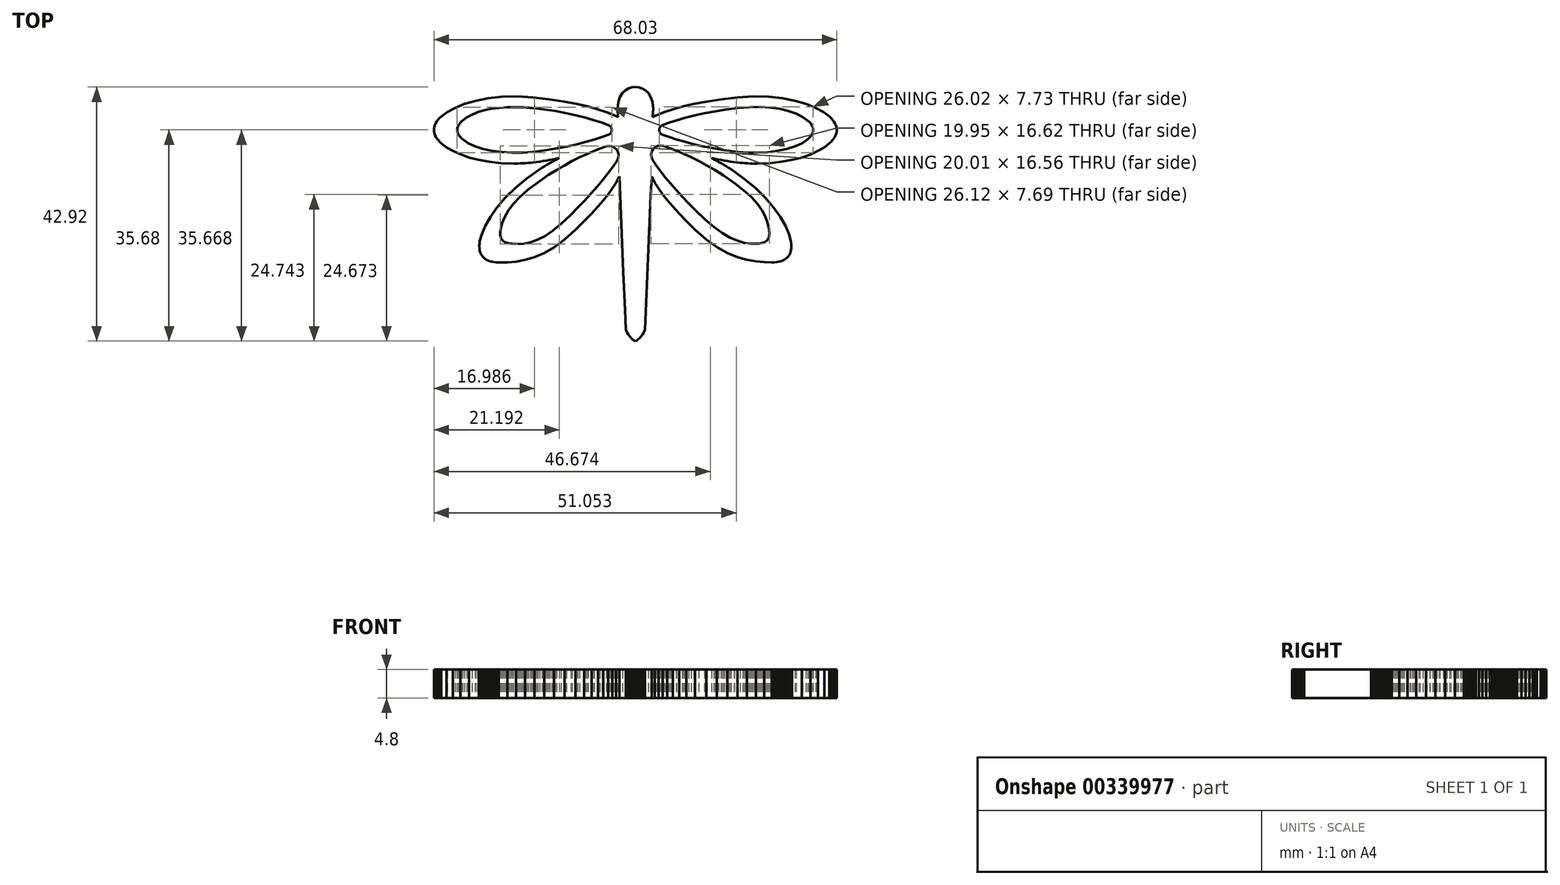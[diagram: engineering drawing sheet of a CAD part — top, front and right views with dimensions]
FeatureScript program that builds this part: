
annotation { "Feature Type Name" : "Feature", "Feature Type Description" : "" }
export const myFeature = defineFeature(function(context is Context, id is Id, definition is map)
    precondition{}
    {
        {
            var Q0;
            Q0=qCreatedBy(makeId("Top.planeOp"),FACE);
            var sketch = newSketch(context, id + "F0", { "sketchPlane" : qUnion([Q0])});
            skLineSegment(sketch, "E0", {"start": v(-35.15, 57.57) * mm, "end": v(-29.95, 57.76) * mm});
            skLineSegment(sketch, "E1", {"start": v(-29.95, 57.76) * mm, "end": v(-25.07, 58.28) * mm});
            skLineSegment(sketch, "E2", {"start": v(-25.07, 58.28) * mm, "end": v(-20.56, 59.1) * mm});
            skLineSegment(sketch, "E3", {"start": v(-20.56, 59.1) * mm, "end": v(-16.45, 60.17) * mm});
            skLineSegment(sketch, "E4", {"start": v(-16.45, 60.17) * mm, "end": v(-12.79, 61.45) * mm});
            skLineSegment(sketch, "E5", {"start": v(-12.79, 61.45) * mm, "end": v(-9.6, 62.89) * mm});
            skLineSegment(sketch, "E6", {"start": v(-9.6, 62.89) * mm, "end": v(-6.9, 64.45) * mm});
            skLineSegment(sketch, "E7", {"start": v(-6.9, 64.45) * mm, "end": v(-4.77, 66.09) * mm});
            skLineSegment(sketch, "E8", {"start": v(-4.77, 66.09) * mm, "end": v(-4.05, 66.78) * mm});
            skLineSegment(sketch, "E9", {"start": v(-4.05, 66.78) * mm, "end": v(-3.43, 67.48) * mm});
            skLineSegment(sketch, "E10", {"start": v(-3.43, 67.48) * mm, "end": v(-2.9, 68.2) * mm});
            skLineSegment(sketch, "E11", {"start": v(-2.9, 68.2) * mm, "end": v(-2.45, 68.9) * mm});
            skLineSegment(sketch, "E12", {"start": v(-2.45, 68.9) * mm, "end": v(-2.1, 69.62) * mm});
            skLineSegment(sketch, "E13", {"start": v(-2.1, 69.62) * mm, "end": v(-1.86, 70.34) * mm});
            skLineSegment(sketch, "E14", {"start": v(-1.86, 70.34) * mm, "end": v(-1.71, 71.06) * mm});
            skLineSegment(sketch, "E15", {"start": v(-1.71, 71.06) * mm, "end": v(-1.66, 71.78) * mm});
            skLineSegment(sketch, "E16", {"start": v(-1.66, 71.78) * mm, "end": v(-1.71, 72.48) * mm});
            skLineSegment(sketch, "E17", {"start": v(-1.71, 72.48) * mm, "end": v(-1.86, 73.2) * mm});
            skLineSegment(sketch, "E18", {"start": v(-1.86, 73.2) * mm, "end": v(-2.1, 73.9) * mm});
            skLineSegment(sketch, "E19", {"start": v(-2.1, 73.9) * mm, "end": v(-2.43, 74.61) * mm});
            skLineSegment(sketch, "E20", {"start": v(-2.43, 74.61) * mm, "end": v(-2.86, 75.32) * mm});
            skLineSegment(sketch, "E21", {"start": v(-2.86, 75.32) * mm, "end": v(-3.38, 76.02) * mm});
            skLineSegment(sketch, "E22", {"start": v(-3.38, 76.02) * mm, "end": v(-4, 76.7) * mm});
            skLineSegment(sketch, "E23", {"start": v(-4, 76.7) * mm, "end": v(-4.7, 77.39) * mm});
            skLineSegment(sketch, "E24", {"start": v(-4.7, 77.39) * mm, "end": v(-7.25, 79.3) * mm});
            skLineSegment(sketch, "E25", {"start": v(-7.25, 79.3) * mm, "end": v(-10.58, 81.11) * mm});
            skLineSegment(sketch, "E26", {"start": v(-10.58, 81.11) * mm, "end": v(-14.63, 82.73) * mm});
            skLineSegment(sketch, "E27", {"start": v(-14.63, 82.73) * mm, "end": v(-19.33, 84.1) * mm});
            skLineSegment(sketch, "E28", {"start": v(-19.33, 84.1) * mm, "end": v(-24.63, 85.12) * mm});
            skLineSegment(sketch, "E29", {"start": v(-24.63, 85.12) * mm, "end": v(-30.46, 85.75) * mm});
            skLineSegment(sketch, "E30", {"start": v(-30.46, 85.75) * mm, "end": v(-36.78, 85.9) * mm});
            skLineSegment(sketch, "E31", {"start": v(-36.78, 85.9) * mm, "end": v(-43.52, 85.52) * mm});
            skLineSegment(sketch, "E32", {"start": v(-43.52, 85.52) * mm, "end": v(-50.3, 84.72) * mm});
            skLineSegment(sketch, "E33", {"start": v(-50.3, 84.72) * mm, "end": v(-56.44, 83.78) * mm});
            skLineSegment(sketch, "E34", {"start": v(-56.44, 83.78) * mm, "end": v(-61.95, 82.73) * mm});
            skLineSegment(sketch, "E35", {"start": v(-61.95, 82.73) * mm, "end": v(-66.8, 81.61) * mm});
            skLineSegment(sketch, "E36", {"start": v(-66.8, 81.61) * mm, "end": v(-70.97, 80.47) * mm});
            skLineSegment(sketch, "E37", {"start": v(-70.97, 80.47) * mm, "end": v(-74.47, 79.34) * mm});
            skLineSegment(sketch, "E38", {"start": v(-74.47, 79.34) * mm, "end": v(-77.28, 78.26) * mm});
            skLineSegment(sketch, "E39", {"start": v(-77.28, 78.26) * mm, "end": v(-79.38, 77.3) * mm});
            skLineSegment(sketch, "E40", {"start": v(-79.38, 77.3) * mm, "end": v(-79.2, 80.74) * mm});
            skLineSegment(sketch, "E41", {"start": v(-79.2, 80.74) * mm, "end": v(-79.5, 83.53) * mm});
            skLineSegment(sketch, "E42", {"start": v(-79.5, 83.53) * mm, "end": v(-80.22, 85.73) * mm});
            skLineSegment(sketch, "E43", {"start": v(-80.22, 85.73) * mm, "end": v(-81.26, 87.4) * mm});
            skLineSegment(sketch, "E44", {"start": v(-81.26, 87.4) * mm, "end": v(-82.52, 88.6) * mm});
            skLineSegment(sketch, "E45", {"start": v(-82.52, 88.6) * mm, "end": v(-83.9, 89.37) * mm});
            skLineSegment(sketch, "E46", {"start": v(-83.9, 89.37) * mm, "end": v(-85.33, 89.8) * mm});
            skLineSegment(sketch, "E47", {"start": v(-85.33, 89.8) * mm, "end": v(-86.7, 89.92) * mm});
            skLineSegment(sketch, "E48", {"start": v(-86.7, 89.92) * mm, "end": v(-88.09, 89.79) * mm});
            skLineSegment(sketch, "E49", {"start": v(-88.09, 89.79) * mm, "end": v(-89.53, 89.35) * mm});
            skLineSegment(sketch, "E50", {"start": v(-89.53, 89.35) * mm, "end": v(-90.93, 88.55) * mm});
            skLineSegment(sketch, "E51", {"start": v(-90.93, 88.55) * mm, "end": v(-92.2, 87.34) * mm});
            skLineSegment(sketch, "E52", {"start": v(-92.2, 87.34) * mm, "end": v(-93.23, 85.66) * mm});
            skLineSegment(sketch, "E53", {"start": v(-93.23, 85.66) * mm, "end": v(-93.94, 83.46) * mm});
            skLineSegment(sketch, "E54", {"start": v(-93.94, 83.46) * mm, "end": v(-94.23, 80.7) * mm});
            skLineSegment(sketch, "E55", {"start": v(-94.23, 80.7) * mm, "end": v(-94.02, 77.3) * mm});
            skLineSegment(sketch, "E56", {"start": v(-94.02, 77.3) * mm, "end": v(-96.12, 78.27) * mm});
            skLineSegment(sketch, "E57", {"start": v(-96.12, 78.27) * mm, "end": v(-98.93, 79.34) * mm});
            skLineSegment(sketch, "E58", {"start": v(-98.93, 79.34) * mm, "end": v(-102.43, 80.47) * mm});
            skLineSegment(sketch, "E59", {"start": v(-102.43, 80.47) * mm, "end": v(-106.6, 81.61) * mm});
            skLineSegment(sketch, "E60", {"start": v(-106.6, 81.61) * mm, "end": v(-111.46, 82.73) * mm});
            skLineSegment(sketch, "E61", {"start": v(-111.46, 82.73) * mm, "end": v(-116.96, 83.78) * mm});
            skLineSegment(sketch, "E62", {"start": v(-116.96, 83.78) * mm, "end": v(-123.1, 84.73) * mm});
            skLineSegment(sketch, "E63", {"start": v(-123.1, 84.73) * mm, "end": v(-129.89, 85.52) * mm});
            skLineSegment(sketch, "E64", {"start": v(-129.89, 85.52) * mm, "end": v(-136.62, 85.91) * mm});
            skLineSegment(sketch, "E65", {"start": v(-136.62, 85.91) * mm, "end": v(-142.94, 85.76) * mm});
            skLineSegment(sketch, "E66", {"start": v(-142.94, 85.76) * mm, "end": v(-148.77, 85.13) * mm});
            skLineSegment(sketch, "E67", {"start": v(-148.77, 85.13) * mm, "end": v(-154.07, 84.1) * mm});
            skLineSegment(sketch, "E68", {"start": v(-154.07, 84.1) * mm, "end": v(-158.77, 82.73) * mm});
            skLineSegment(sketch, "E69", {"start": v(-158.77, 82.73) * mm, "end": v(-162.82, 81.11) * mm});
            skLineSegment(sketch, "E70", {"start": v(-162.82, 81.11) * mm, "end": v(-166.15, 79.3) * mm});
            skLineSegment(sketch, "E71", {"start": v(-166.15, 79.3) * mm, "end": v(-168.71, 77.39) * mm});
            skLineSegment(sketch, "E72", {"start": v(-168.71, 77.39) * mm, "end": v(-169.41, 76.7) * mm});
            skLineSegment(sketch, "E73", {"start": v(-169.41, 76.7) * mm, "end": v(-170.02, 76.02) * mm});
            skLineSegment(sketch, "E74", {"start": v(-170.02, 76.02) * mm, "end": v(-170.54, 75.32) * mm});
            skLineSegment(sketch, "E75", {"start": v(-170.54, 75.32) * mm, "end": v(-170.97, 74.61) * mm});
            skLineSegment(sketch, "E76", {"start": v(-170.97, 74.61) * mm, "end": v(-171.3, 73.9) * mm});
            skLineSegment(sketch, "E77", {"start": v(-171.3, 73.9) * mm, "end": v(-171.55, 73.2) * mm});
            skLineSegment(sketch, "E78", {"start": v(-171.55, 73.2) * mm, "end": v(-171.7, 72.48) * mm});
            skLineSegment(sketch, "E79", {"start": v(-171.7, 72.48) * mm, "end": v(-171.74, 71.78) * mm});
            skLineSegment(sketch, "E80", {"start": v(-171.74, 71.78) * mm, "end": v(-171.7, 71.06) * mm});
            skLineSegment(sketch, "E81", {"start": v(-171.7, 71.06) * mm, "end": v(-171.54, 70.34) * mm});
            skLineSegment(sketch, "E82", {"start": v(-171.54, 70.34) * mm, "end": v(-171.3, 69.62) * mm});
            skLineSegment(sketch, "E83", {"start": v(-171.3, 69.62) * mm, "end": v(-170.95, 68.9) * mm});
            skLineSegment(sketch, "E84", {"start": v(-170.95, 68.9) * mm, "end": v(-170.51, 68.2) * mm});
            skLineSegment(sketch, "E85", {"start": v(-170.51, 68.2) * mm, "end": v(-169.98, 67.48) * mm});
            skLineSegment(sketch, "E86", {"start": v(-169.98, 67.48) * mm, "end": v(-169.35, 66.78) * mm});
            skLineSegment(sketch, "E87", {"start": v(-169.35, 66.78) * mm, "end": v(-168.63, 66.1) * mm});
            skLineSegment(sketch, "E88", {"start": v(-168.63, 66.1) * mm, "end": v(-166.5, 64.45) * mm});
            skLineSegment(sketch, "E89", {"start": v(-166.5, 64.45) * mm, "end": v(-163.81, 62.89) * mm});
            skLineSegment(sketch, "E90", {"start": v(-163.81, 62.89) * mm, "end": v(-160.62, 61.45) * mm});
            skLineSegment(sketch, "E91", {"start": v(-160.62, 61.45) * mm, "end": v(-156.95, 60.17) * mm});
            skLineSegment(sketch, "E92", {"start": v(-156.95, 60.17) * mm, "end": v(-152.84, 59.1) * mm});
            skLineSegment(sketch, "E93", {"start": v(-152.84, 59.1) * mm, "end": v(-148.33, 58.28) * mm});
            skLineSegment(sketch, "E94", {"start": v(-148.33, 58.28) * mm, "end": v(-143.46, 57.76) * mm});
            skLineSegment(sketch, "E95", {"start": v(-143.46, 57.76) * mm, "end": v(-138.25, 57.58) * mm});
            skLineSegment(sketch, "E96", {"start": v(-138.25, 57.58) * mm, "end": v(-137.24, 57.58) * mm});
            skLineSegment(sketch, "E97", {"start": v(-137.24, 57.58) * mm, "end": v(-136.21, 57.6) * mm});
            skLineSegment(sketch, "E98", {"start": v(-136.21, 57.6) * mm, "end": v(-135.18, 57.64) * mm});
            skLineSegment(sketch, "E99", {"start": v(-135.18, 57.64) * mm, "end": v(-134.14, 57.69) * mm});
            skLineSegment(sketch, "E100", {"start": v(-134.14, 57.69) * mm, "end": v(-133.09, 57.75) * mm});
            skLineSegment(sketch, "E101", {"start": v(-133.09, 57.75) * mm, "end": v(-132.02, 57.83) * mm});
            skLineSegment(sketch, "E102", {"start": v(-132.02, 57.83) * mm, "end": v(-130.95, 57.92) * mm});
            skLineSegment(sketch, "E103", {"start": v(-130.95, 57.92) * mm, "end": v(-129.88, 58.03) * mm});
            skLineSegment(sketch, "E104", {"start": v(-129.88, 58.03) * mm, "end": v(-128.45, 58.2) * mm});
            skLineSegment(sketch, "E105", {"start": v(-128.45, 58.2) * mm, "end": v(-127.03, 58.39) * mm});
            skLineSegment(sketch, "E106", {"start": v(-127.03, 58.39) * mm, "end": v(-125.62, 58.6) * mm});
            skLineSegment(sketch, "E107", {"start": v(-125.62, 58.6) * mm, "end": v(-124.23, 58.82) * mm});
            skLineSegment(sketch, "E108", {"start": v(-124.23, 58.82) * mm, "end": v(-122.85, 59.07) * mm});
            skLineSegment(sketch, "E109", {"start": v(-122.85, 59.07) * mm, "end": v(-121.49, 59.33) * mm});
            skLineSegment(sketch, "E110", {"start": v(-121.49, 59.33) * mm, "end": v(-120.14, 59.6) * mm});
            skLineSegment(sketch, "E111", {"start": v(-120.14, 59.6) * mm, "end": v(-118.8, 59.9) * mm});
            skLineSegment(sketch, "E112", {"start": v(-118.8, 59.9) * mm, "end": v(-119.84, 59.36) * mm});
            skLineSegment(sketch, "E113", {"start": v(-119.84, 59.36) * mm, "end": v(-120.87, 58.81) * mm});
            skLineSegment(sketch, "E114", {"start": v(-120.87, 58.81) * mm, "end": v(-121.9, 58.24) * mm});
            skLineSegment(sketch, "E115", {"start": v(-121.9, 58.24) * mm, "end": v(-122.94, 57.66) * mm});
            skLineSegment(sketch, "E116", {"start": v(-122.94, 57.66) * mm, "end": v(-123.98, 57.06) * mm});
            skLineSegment(sketch, "E117", {"start": v(-123.98, 57.06) * mm, "end": v(-125, 56.45) * mm});
            skLineSegment(sketch, "E118", {"start": v(-125, 56.45) * mm, "end": v(-126.04, 55.81) * mm});
            skLineSegment(sketch, "E119", {"start": v(-126.04, 55.81) * mm, "end": v(-127.06, 55.16) * mm});
            skLineSegment(sketch, "E120", {"start": v(-127.06, 55.16) * mm, "end": v(-132.58, 51.27) * mm});
            skLineSegment(sketch, "E121", {"start": v(-132.58, 51.27) * mm, "end": v(-137.43, 47.22) * mm});
            skLineSegment(sketch, "E122", {"start": v(-137.43, 47.22) * mm, "end": v(-141.6, 43.1) * mm});
            skLineSegment(sketch, "E123", {"start": v(-141.6, 43.1) * mm, "end": v(-145.1, 38.99) * mm});
            skLineSegment(sketch, "E124", {"start": v(-145.1, 38.99) * mm, "end": v(-147.94, 35) * mm});
            skLineSegment(sketch, "E125", {"start": v(-147.94, 35) * mm, "end": v(-150.1, 31.21) * mm});
            skLineSegment(sketch, "E126", {"start": v(-150.1, 31.21) * mm, "end": v(-151.58, 27.72) * mm});
            skLineSegment(sketch, "E127", {"start": v(-151.58, 27.72) * mm, "end": v(-152.39, 24.63) * mm});
            skLineSegment(sketch, "E128", {"start": v(-152.39, 24.63) * mm, "end": v(-152.51, 23.66) * mm});
            skLineSegment(sketch, "E129", {"start": v(-152.51, 23.66) * mm, "end": v(-152.56, 22.74) * mm});
            skLineSegment(sketch, "E130", {"start": v(-152.56, 22.74) * mm, "end": v(-152.53, 21.87) * mm});
            skLineSegment(sketch, "E131", {"start": v(-152.53, 21.87) * mm, "end": v(-152.43, 21.05) * mm});
            skLineSegment(sketch, "E132", {"start": v(-152.43, 21.05) * mm, "end": v(-152.25, 20.29) * mm});
            skLineSegment(sketch, "E133", {"start": v(-152.25, 20.29) * mm, "end": v(-152, 19.58) * mm});
            skLineSegment(sketch, "E134", {"start": v(-152, 19.58) * mm, "end": v(-151.67, 18.93) * mm});
            skLineSegment(sketch, "E135", {"start": v(-151.67, 18.93) * mm, "end": v(-151.27, 18.35) * mm});
            skLineSegment(sketch, "E136", {"start": v(-151.27, 18.35) * mm, "end": v(-150.78, 17.82) * mm});
            skLineSegment(sketch, "E137", {"start": v(-150.78, 17.82) * mm, "end": v(-150.22, 17.35) * mm});
            skLineSegment(sketch, "E138", {"start": v(-150.22, 17.35) * mm, "end": v(-149.58, 16.95) * mm});
            skLineSegment(sketch, "E139", {"start": v(-149.58, 16.95) * mm, "end": v(-148.86, 16.6) * mm});
            skLineSegment(sketch, "E140", {"start": v(-148.86, 16.6) * mm, "end": v(-148.07, 16.31) * mm});
            skLineSegment(sketch, "E141", {"start": v(-148.07, 16.31) * mm, "end": v(-147.21, 16.09) * mm});
            skLineSegment(sketch, "E142", {"start": v(-147.21, 16.09) * mm, "end": v(-146.29, 15.93) * mm});
            skLineSegment(sketch, "E143", {"start": v(-146.29, 15.93) * mm, "end": v(-145.3, 15.83) * mm});
            skLineSegment(sketch, "E144", {"start": v(-145.3, 15.83) * mm, "end": v(-145.18, 15.83) * mm});
            skLineSegment(sketch, "E145", {"start": v(-145.18, 15.83) * mm, "end": v(-145.06, 15.82) * mm});
            skLineSegment(sketch, "E146", {"start": v(-145.06, 15.82) * mm, "end": v(-144.94, 15.82) * mm});
            skLineSegment(sketch, "E147", {"start": v(-144.94, 15.82) * mm, "end": v(-144.82, 15.81) * mm});
            skLineSegment(sketch, "E148", {"start": v(-144.82, 15.81) * mm, "end": v(-144.7, 15.81) * mm});
            skLineSegment(sketch, "E149", {"start": v(-144.7, 15.81) * mm, "end": v(-144.57, 15.8) * mm});
            skLineSegment(sketch, "E150", {"start": v(-144.57, 15.8) * mm, "end": v(-144.45, 15.8) * mm});
            skLineSegment(sketch, "E151", {"start": v(-144.45, 15.8) * mm, "end": v(-144.32, 15.8) * mm});
            skLineSegment(sketch, "E152", {"start": v(-144.32, 15.8) * mm, "end": v(-140.72, 15.84) * mm});
            skLineSegment(sketch, "E153", {"start": v(-140.72, 15.84) * mm, "end": v(-137.02, 16.15) * mm});
            skLineSegment(sketch, "E154", {"start": v(-137.02, 16.15) * mm, "end": v(-133.21, 16.84) * mm});
            skLineSegment(sketch, "E155", {"start": v(-133.21, 16.84) * mm, "end": v(-129.28, 18.02) * mm});
            skLineSegment(sketch, "E156", {"start": v(-129.28, 18.02) * mm, "end": v(-125.2, 19.78) * mm});
            skLineSegment(sketch, "E157", {"start": v(-125.2, 19.78) * mm, "end": v(-120.96, 22.23) * mm});
            skLineSegment(sketch, "E158", {"start": v(-120.96, 22.23) * mm, "end": v(-116.55, 25.49) * mm});
            skLineSegment(sketch, "E159", {"start": v(-116.55, 25.49) * mm, "end": v(-111.95, 29.65) * mm});
            skLineSegment(sketch, "E160", {"start": v(-111.95, 29.65) * mm, "end": v(-108.3, 33.29) * mm});
            skLineSegment(sketch, "E161", {"start": v(-108.3, 33.29) * mm, "end": v(-105.17, 36.52) * mm});
            skLineSegment(sketch, "E162", {"start": v(-105.17, 36.52) * mm, "end": v(-102.48, 39.42) * mm});
            skLineSegment(sketch, "E163", {"start": v(-102.48, 39.42) * mm, "end": v(-100.17, 42.08) * mm});
            skLineSegment(sketch, "E164", {"start": v(-100.17, 42.08) * mm, "end": v(-98.18, 44.59) * mm});
            skLineSegment(sketch, "E165", {"start": v(-98.18, 44.59) * mm, "end": v(-96.45, 47.03) * mm});
            skLineSegment(sketch, "E166", {"start": v(-96.45, 47.03) * mm, "end": v(-94.9, 49.5) * mm});
            skLineSegment(sketch, "E167", {"start": v(-94.9, 49.5) * mm, "end": v(-93.48, 52.09) * mm});
            skLineSegment(sketch, "E168", {"start": v(-93.48, 52.09) * mm, "end": v(-93.14, 44.02) * mm});
            skLineSegment(sketch, "E169", {"start": v(-93.14, 44.02) * mm, "end": v(-92.8, 35.96) * mm});
            skLineSegment(sketch, "E170", {"start": v(-92.8, 35.96) * mm, "end": v(-92.45, 27.9) * mm});
            skLineSegment(sketch, "E171", {"start": v(-92.45, 27.9) * mm, "end": v(-92.1, 19.83) * mm});
            skLineSegment(sketch, "E172", {"start": v(-92.1, 19.83) * mm, "end": v(-91.76, 11.77) * mm});
            skLineSegment(sketch, "E173", {"start": v(-91.76, 11.77) * mm, "end": v(-91.42, 3.7) * mm});
            skLineSegment(sketch, "E174", {"start": v(-91.42, 3.7) * mm, "end": v(-91.08, -4.36) * mm});
            skLineSegment(sketch, "E175", {"start": v(-91.08, -4.36) * mm, "end": v(-90.74, -12.42) * mm});
            skLineSegment(sketch, "E176", {"start": v(-90.74, -12.42) * mm, "end": v(-90.61, -12.95) * mm});
            skLineSegment(sketch, "E177", {"start": v(-90.61, -12.95) * mm, "end": v(-90.27, -13.65) * mm});
            skLineSegment(sketch, "E178", {"start": v(-90.27, -13.65) * mm, "end": v(-89.76, -14.47) * mm});
            skLineSegment(sketch, "E179", {"start": v(-89.76, -14.47) * mm, "end": v(-89.14, -15.3) * mm});
            skLineSegment(sketch, "E180", {"start": v(-89.14, -15.3) * mm, "end": v(-88.47, -16.1) * mm});
            skLineSegment(sketch, "E181", {"start": v(-88.47, -16.1) * mm, "end": v(-87.79, -16.76) * mm});
            skLineSegment(sketch, "E182", {"start": v(-87.79, -16.76) * mm, "end": v(-87.15, -17.22) * mm});
            skLineSegment(sketch, "E183", {"start": v(-87.15, -17.22) * mm, "end": v(-86.62, -17.38) * mm});
            skLineSegment(sketch, "E184", {"start": v(-86.62, -17.38) * mm, "end": v(-86.14, -17.22) * mm});
            skLineSegment(sketch, "E185", {"start": v(-86.14, -17.22) * mm, "end": v(-85.55, -16.76) * mm});
            skLineSegment(sketch, "E186", {"start": v(-85.55, -16.76) * mm, "end": v(-84.9, -16.1) * mm});
            skLineSegment(sketch, "E187", {"start": v(-84.9, -16.1) * mm, "end": v(-84.24, -15.3) * mm});
            skLineSegment(sketch, "E188", {"start": v(-84.24, -15.3) * mm, "end": v(-83.63, -14.47) * mm});
            skLineSegment(sketch, "E189", {"start": v(-83.63, -14.47) * mm, "end": v(-83.13, -13.65) * mm});
            skLineSegment(sketch, "E190", {"start": v(-83.13, -13.65) * mm, "end": v(-82.79, -12.95) * mm});
            skLineSegment(sketch, "E191", {"start": v(-82.79, -12.95) * mm, "end": v(-82.66, -12.42) * mm});
            skLineSegment(sketch, "E192", {"start": v(-82.66, -12.42) * mm, "end": v(-82.3, -4.36) * mm});
            skLineSegment(sketch, "E193", {"start": v(-82.3, -4.36) * mm, "end": v(-81.95, 3.7) * mm});
            skLineSegment(sketch, "E194", {"start": v(-81.95, 3.7) * mm, "end": v(-81.6, 11.77) * mm});
            skLineSegment(sketch, "E195", {"start": v(-81.6, 11.77) * mm, "end": v(-81.25, 19.84) * mm});
            skLineSegment(sketch, "E196", {"start": v(-81.25, 19.84) * mm, "end": v(-80.9, 27.9) * mm});
            skLineSegment(sketch, "E197", {"start": v(-80.9, 27.9) * mm, "end": v(-80.54, 35.97) * mm});
            skLineSegment(sketch, "E198", {"start": v(-80.54, 35.97) * mm, "end": v(-80.18, 44.03) * mm});
            skLineSegment(sketch, "E199", {"start": v(-80.18, 44.03) * mm, "end": v(-79.83, 52.1) * mm});
            skLineSegment(sketch, "E200", {"start": v(-79.83, 52.1) * mm, "end": v(-78.41, 49.51) * mm});
            skLineSegment(sketch, "E201", {"start": v(-78.41, 49.51) * mm, "end": v(-76.88, 47.04) * mm});
            skLineSegment(sketch, "E202", {"start": v(-76.88, 47.04) * mm, "end": v(-75.16, 44.6) * mm});
            skLineSegment(sketch, "E203", {"start": v(-75.16, 44.6) * mm, "end": v(-73.18, 42.08) * mm});
            skLineSegment(sketch, "E204", {"start": v(-73.18, 42.08) * mm, "end": v(-70.9, 39.42) * mm});
            skLineSegment(sketch, "E205", {"start": v(-70.9, 39.42) * mm, "end": v(-68.22, 36.52) * mm});
            skLineSegment(sketch, "E206", {"start": v(-68.22, 36.52) * mm, "end": v(-65.1, 33.3) * mm});
            skLineSegment(sketch, "E207", {"start": v(-65.1, 33.3) * mm, "end": v(-61.45, 29.65) * mm});
            skLineSegment(sketch, "E208", {"start": v(-61.45, 29.65) * mm, "end": v(-56.8, 25.5) * mm});
            skLineSegment(sketch, "E209", {"start": v(-56.8, 25.5) * mm, "end": v(-52.24, 22.26) * mm});
            skLineSegment(sketch, "E210", {"start": v(-52.24, 22.26) * mm, "end": v(-47.82, 19.82) * mm});
            skLineSegment(sketch, "E211", {"start": v(-47.82, 19.82) * mm, "end": v(-43.58, 18.08) * mm});
            skLineSegment(sketch, "E212", {"start": v(-43.58, 18.08) * mm, "end": v(-39.55, 16.92) * mm});
            skLineSegment(sketch, "E213", {"start": v(-39.55, 16.92) * mm, "end": v(-35.77, 16.23) * mm});
            skLineSegment(sketch, "E214", {"start": v(-35.77, 16.23) * mm, "end": v(-32.27, 15.9) * mm});
            skLineSegment(sketch, "E215", {"start": v(-32.27, 15.9) * mm, "end": v(-29.08, 15.8) * mm});
            skLineSegment(sketch, "E216", {"start": v(-29.08, 15.8) * mm, "end": v(-28.95, 15.8) * mm});
            skLineSegment(sketch, "E217", {"start": v(-28.95, 15.8) * mm, "end": v(-28.83, 15.8) * mm});
            skLineSegment(sketch, "E218", {"start": v(-28.83, 15.8) * mm, "end": v(-28.7, 15.81) * mm});
            skLineSegment(sketch, "E219", {"start": v(-28.7, 15.81) * mm, "end": v(-28.58, 15.81) * mm});
            skLineSegment(sketch, "E220", {"start": v(-28.58, 15.81) * mm, "end": v(-28.46, 15.82) * mm});
            skLineSegment(sketch, "E221", {"start": v(-28.46, 15.82) * mm, "end": v(-28.34, 15.82) * mm});
            skLineSegment(sketch, "E222", {"start": v(-28.34, 15.82) * mm, "end": v(-28.22, 15.83) * mm});
            skLineSegment(sketch, "E223", {"start": v(-28.22, 15.83) * mm, "end": v(-28.1, 15.83) * mm});
            skLineSegment(sketch, "E224", {"start": v(-28.1, 15.83) * mm, "end": v(-27.11, 15.93) * mm});
            skLineSegment(sketch, "E225", {"start": v(-27.11, 15.93) * mm, "end": v(-26.18, 16.09) * mm});
            skLineSegment(sketch, "E226", {"start": v(-26.18, 16.09) * mm, "end": v(-25.33, 16.31) * mm});
            skLineSegment(sketch, "E227", {"start": v(-25.33, 16.31) * mm, "end": v(-24.54, 16.6) * mm});
            skLineSegment(sketch, "E228", {"start": v(-24.54, 16.6) * mm, "end": v(-23.82, 16.95) * mm});
            skLineSegment(sketch, "E229", {"start": v(-23.82, 16.95) * mm, "end": v(-23.18, 17.35) * mm});
            skLineSegment(sketch, "E230", {"start": v(-23.18, 17.35) * mm, "end": v(-22.61, 17.82) * mm});
            skLineSegment(sketch, "E231", {"start": v(-22.61, 17.82) * mm, "end": v(-22.13, 18.35) * mm});
            skLineSegment(sketch, "E232", {"start": v(-22.13, 18.35) * mm, "end": v(-21.73, 18.93) * mm});
            skLineSegment(sketch, "E233", {"start": v(-21.73, 18.93) * mm, "end": v(-21.4, 19.58) * mm});
            skLineSegment(sketch, "E234", {"start": v(-21.4, 19.58) * mm, "end": v(-21.15, 20.29) * mm});
            skLineSegment(sketch, "E235", {"start": v(-21.15, 20.29) * mm, "end": v(-20.97, 21.05) * mm});
            skLineSegment(sketch, "E236", {"start": v(-20.97, 21.05) * mm, "end": v(-20.86, 21.87) * mm});
            skLineSegment(sketch, "E237", {"start": v(-20.86, 21.87) * mm, "end": v(-20.84, 22.74) * mm});
            skLineSegment(sketch, "E238", {"start": v(-20.84, 22.74) * mm, "end": v(-20.88, 23.66) * mm});
            skLineSegment(sketch, "E239", {"start": v(-20.88, 23.66) * mm, "end": v(-21, 24.63) * mm});
            skLineSegment(sketch, "E240", {"start": v(-21, 24.63) * mm, "end": v(-21.82, 27.72) * mm});
            skLineSegment(sketch, "E241", {"start": v(-21.82, 27.72) * mm, "end": v(-23.3, 31.2) * mm});
            skLineSegment(sketch, "E242", {"start": v(-23.3, 31.2) * mm, "end": v(-25.46, 35) * mm});
            skLineSegment(sketch, "E243", {"start": v(-25.46, 35) * mm, "end": v(-28.3, 38.99) * mm});
            skLineSegment(sketch, "E244", {"start": v(-28.3, 38.99) * mm, "end": v(-31.8, 43.1) * mm});
            skLineSegment(sketch, "E245", {"start": v(-31.8, 43.1) * mm, "end": v(-35.97, 47.22) * mm});
            skLineSegment(sketch, "E246", {"start": v(-35.97, 47.22) * mm, "end": v(-40.82, 51.27) * mm});
            skLineSegment(sketch, "E247", {"start": v(-40.82, 51.27) * mm, "end": v(-46.34, 55.16) * mm});
            skLineSegment(sketch, "E248", {"start": v(-46.34, 55.16) * mm, "end": v(-47.36, 55.8) * mm});
            skLineSegment(sketch, "E249", {"start": v(-47.36, 55.8) * mm, "end": v(-48.4, 56.44) * mm});
            skLineSegment(sketch, "E250", {"start": v(-48.4, 56.44) * mm, "end": v(-49.42, 57.06) * mm});
            skLineSegment(sketch, "E251", {"start": v(-49.42, 57.06) * mm, "end": v(-50.46, 57.66) * mm});
            skLineSegment(sketch, "E252", {"start": v(-50.46, 57.66) * mm, "end": v(-51.5, 58.24) * mm});
            skLineSegment(sketch, "E253", {"start": v(-51.5, 58.24) * mm, "end": v(-52.53, 58.8) * mm});
            skLineSegment(sketch, "E254", {"start": v(-52.53, 58.8) * mm, "end": v(-53.56, 59.36) * mm});
            skLineSegment(sketch, "E255", {"start": v(-53.56, 59.36) * mm, "end": v(-54.6, 59.9) * mm});
            skLineSegment(sketch, "E256", {"start": v(-54.6, 59.9) * mm, "end": v(-53.26, 59.6) * mm});
            skLineSegment(sketch, "E257", {"start": v(-53.26, 59.6) * mm, "end": v(-51.91, 59.33) * mm});
            skLineSegment(sketch, "E258", {"start": v(-51.91, 59.33) * mm, "end": v(-50.55, 59.07) * mm});
            skLineSegment(sketch, "E259", {"start": v(-50.55, 59.07) * mm, "end": v(-49.17, 58.82) * mm});
            skLineSegment(sketch, "E260", {"start": v(-49.17, 58.82) * mm, "end": v(-47.78, 58.6) * mm});
            skLineSegment(sketch, "E261", {"start": v(-47.78, 58.6) * mm, "end": v(-46.37, 58.39) * mm});
            skLineSegment(sketch, "E262", {"start": v(-46.37, 58.39) * mm, "end": v(-44.95, 58.2) * mm});
            skLineSegment(sketch, "E263", {"start": v(-44.95, 58.2) * mm, "end": v(-43.52, 58.03) * mm});
            skLineSegment(sketch, "E264", {"start": v(-43.52, 58.03) * mm, "end": v(-42.45, 57.92) * mm});
            skLineSegment(sketch, "E265", {"start": v(-42.45, 57.92) * mm, "end": v(-41.38, 57.83) * mm});
            skLineSegment(sketch, "E266", {"start": v(-41.38, 57.83) * mm, "end": v(-40.32, 57.75) * mm});
            skLineSegment(sketch, "E267", {"start": v(-40.32, 57.75) * mm, "end": v(-39.27, 57.69) * mm});
            skLineSegment(sketch, "E268", {"start": v(-39.27, 57.69) * mm, "end": v(-38.22, 57.64) * mm});
            skLineSegment(sketch, "E269", {"start": v(-38.22, 57.64) * mm, "end": v(-37.2, 57.6) * mm});
            skLineSegment(sketch, "E270", {"start": v(-37.2, 57.6) * mm, "end": v(-36.17, 57.58) * mm});
            skLineSegment(sketch, "E271", {"start": v(-36.17, 57.58) * mm, "end": v(-35.15, 57.57) * mm});
            skLineSegment(sketch, "E272", {"start": v(-43.37, 81) * mm, "end": v(-38.63, 81.4) * mm});
            skLineSegment(sketch, "E273", {"start": v(-38.63, 81.4) * mm, "end": v(-34.07, 81.47) * mm});
            skLineSegment(sketch, "E274", {"start": v(-34.07, 81.47) * mm, "end": v(-29.76, 81.23) * mm});
            skLineSegment(sketch, "E275", {"start": v(-29.76, 81.23) * mm, "end": v(-25.74, 80.67) * mm});
            skLineSegment(sketch, "E276", {"start": v(-25.74, 80.67) * mm, "end": v(-22.08, 79.82) * mm});
            skLineSegment(sketch, "E277", {"start": v(-22.08, 79.82) * mm, "end": v(-18.83, 78.7) * mm});
            skLineSegment(sketch, "E278", {"start": v(-18.83, 78.7) * mm, "end": v(-16.05, 77.29) * mm});
            skLineSegment(sketch, "E279", {"start": v(-16.05, 77.29) * mm, "end": v(-13.8, 75.63) * mm});
            skLineSegment(sketch, "E280", {"start": v(-13.8, 75.63) * mm, "end": v(-13.29, 75.14) * mm});
            skLineSegment(sketch, "E281", {"start": v(-13.29, 75.14) * mm, "end": v(-12.84, 74.64) * mm});
            skLineSegment(sketch, "E282", {"start": v(-12.84, 74.64) * mm, "end": v(-12.46, 74.15) * mm});
            skLineSegment(sketch, "E283", {"start": v(-12.46, 74.15) * mm, "end": v(-12.15, 73.66) * mm});
            skLineSegment(sketch, "E284", {"start": v(-12.15, 73.66) * mm, "end": v(-11.9, 73.18) * mm});
            skLineSegment(sketch, "E285", {"start": v(-11.9, 73.18) * mm, "end": v(-11.73, 72.7) * mm});
            skLineSegment(sketch, "E286", {"start": v(-11.73, 72.7) * mm, "end": v(-11.62, 72.24) * mm});
            skLineSegment(sketch, "E287", {"start": v(-11.62, 72.24) * mm, "end": v(-11.58, 71.78) * mm});
            skLineSegment(sketch, "E288", {"start": v(-11.58, 71.78) * mm, "end": v(-11.62, 71.31) * mm});
            skLineSegment(sketch, "E289", {"start": v(-11.62, 71.31) * mm, "end": v(-11.73, 70.84) * mm});
            skLineSegment(sketch, "E290", {"start": v(-11.73, 70.84) * mm, "end": v(-11.91, 70.36) * mm});
            skLineSegment(sketch, "E291", {"start": v(-11.91, 70.36) * mm, "end": v(-12.16, 69.86) * mm});
            skLineSegment(sketch, "E292", {"start": v(-12.16, 69.86) * mm, "end": v(-12.49, 69.37) * mm});
            skLineSegment(sketch, "E293", {"start": v(-12.49, 69.37) * mm, "end": v(-12.88, 68.87) * mm});
            skLineSegment(sketch, "E294", {"start": v(-12.88, 68.87) * mm, "end": v(-13.34, 68.37) * mm});
            skLineSegment(sketch, "E295", {"start": v(-13.34, 68.37) * mm, "end": v(-13.87, 67.86) * mm});
            skLineSegment(sketch, "E296", {"start": v(-13.87, 67.86) * mm, "end": v(-16.25, 66.2) * mm});
            skLineSegment(sketch, "E297", {"start": v(-16.25, 66.2) * mm, "end": v(-19.28, 64.82) * mm});
            skLineSegment(sketch, "E298", {"start": v(-19.28, 64.82) * mm, "end": v(-22.83, 63.73) * mm});
            skLineSegment(sketch, "E299", {"start": v(-22.83, 63.73) * mm, "end": v(-26.74, 62.92) * mm});
            skLineSegment(sketch, "E300", {"start": v(-26.74, 62.92) * mm, "end": v(-30.9, 62.4) * mm});
            skLineSegment(sketch, "E301", {"start": v(-30.9, 62.4) * mm, "end": v(-35.14, 62.16) * mm});
            skLineSegment(sketch, "E302", {"start": v(-35.14, 62.16) * mm, "end": v(-39.34, 62.21) * mm});
            skLineSegment(sketch, "E303", {"start": v(-39.34, 62.21) * mm, "end": v(-43.36, 62.55) * mm});
            skLineSegment(sketch, "E304", {"start": v(-43.36, 62.55) * mm, "end": v(-48.26, 63.16) * mm});
            skLineSegment(sketch, "E305", {"start": v(-48.26, 63.16) * mm, "end": v(-52.99, 63.92) * mm});
            skLineSegment(sketch, "E306", {"start": v(-52.99, 63.92) * mm, "end": v(-57.5, 64.78) * mm});
            skLineSegment(sketch, "E307", {"start": v(-57.5, 64.78) * mm, "end": v(-61.75, 65.72) * mm});
            skLineSegment(sketch, "E308", {"start": v(-61.75, 65.72) * mm, "end": v(-65.7, 66.73) * mm});
            skLineSegment(sketch, "E309", {"start": v(-65.7, 66.73) * mm, "end": v(-69.29, 67.76) * mm});
            skLineSegment(sketch, "E310", {"start": v(-69.29, 67.76) * mm, "end": v(-72.5, 68.8) * mm});
            skLineSegment(sketch, "E311", {"start": v(-72.5, 68.8) * mm, "end": v(-75.27, 69.8) * mm});
            skLineSegment(sketch, "E312", {"start": v(-75.27, 69.8) * mm, "end": v(-75.87, 70.15) * mm});
            skLineSegment(sketch, "E313", {"start": v(-75.87, 70.15) * mm, "end": v(-76.3, 70.63) * mm});
            skLineSegment(sketch, "E314", {"start": v(-76.3, 70.63) * mm, "end": v(-76.56, 71.19) * mm});
            skLineSegment(sketch, "E315", {"start": v(-76.56, 71.19) * mm, "end": v(-76.65, 71.8) * mm});
            skLineSegment(sketch, "E316", {"start": v(-76.65, 71.8) * mm, "end": v(-76.56, 72.4) * mm});
            skLineSegment(sketch, "E317", {"start": v(-76.56, 72.4) * mm, "end": v(-76.3, 72.97) * mm});
            skLineSegment(sketch, "E318", {"start": v(-76.3, 72.97) * mm, "end": v(-75.88, 73.45) * mm});
            skLineSegment(sketch, "E319", {"start": v(-75.88, 73.45) * mm, "end": v(-75.28, 73.8) * mm});
            skLineSegment(sketch, "E320", {"start": v(-75.28, 73.8) * mm, "end": v(-72.51, 74.82) * mm});
            skLineSegment(sketch, "E321", {"start": v(-72.51, 74.82) * mm, "end": v(-69.3, 75.87) * mm});
            skLineSegment(sketch, "E322", {"start": v(-69.3, 75.87) * mm, "end": v(-65.7, 76.9) * mm});
            skLineSegment(sketch, "E323", {"start": v(-65.7, 76.9) * mm, "end": v(-61.76, 77.91) * mm});
            skLineSegment(sketch, "E324", {"start": v(-61.76, 77.91) * mm, "end": v(-57.52, 78.85) * mm});
            skLineSegment(sketch, "E325", {"start": v(-57.52, 78.85) * mm, "end": v(-53, 79.7) * mm});
            skLineSegment(sketch, "E326", {"start": v(-53, 79.7) * mm, "end": v(-48.27, 80.43) * mm});
            skLineSegment(sketch, "E327", {"start": v(-48.27, 80.43) * mm, "end": v(-43.37, 81) * mm});
            skLineSegment(sketch, "E328", {"start": v(-30.93, 25.37) * mm, "end": v(-31.26, 25.02) * mm});
            skLineSegment(sketch, "E329", {"start": v(-31.26, 25.02) * mm, "end": v(-31.64, 24.71) * mm});
            skLineSegment(sketch, "E330", {"start": v(-31.64, 24.71) * mm, "end": v(-32.1, 24.44) * mm});
            skLineSegment(sketch, "E331", {"start": v(-32.1, 24.44) * mm, "end": v(-32.6, 24.21) * mm});
            skLineSegment(sketch, "E332", {"start": v(-32.6, 24.21) * mm, "end": v(-33.18, 24.02) * mm});
            skLineSegment(sketch, "E333", {"start": v(-33.18, 24.02) * mm, "end": v(-33.81, 23.87) * mm});
            skLineSegment(sketch, "E334", {"start": v(-33.81, 23.87) * mm, "end": v(-34.5, 23.76) * mm});
            skLineSegment(sketch, "E335", {"start": v(-34.5, 23.76) * mm, "end": v(-35.23, 23.7) * mm});
            skLineSegment(sketch, "E336", {"start": v(-35.23, 23.7) * mm, "end": v(-37.97, 23.7) * mm});
            skLineSegment(sketch, "E337", {"start": v(-37.97, 23.7) * mm, "end": v(-40.76, 24.11) * mm});
            skLineSegment(sketch, "E338", {"start": v(-40.76, 24.11) * mm, "end": v(-43.64, 24.96) * mm});
            skLineSegment(sketch, "E339", {"start": v(-43.64, 24.96) * mm, "end": v(-46.67, 26.3) * mm});
            skLineSegment(sketch, "E340", {"start": v(-46.67, 26.3) * mm, "end": v(-49.9, 28.21) * mm});
            skLineSegment(sketch, "E341", {"start": v(-49.9, 28.21) * mm, "end": v(-53.37, 30.72) * mm});
            skLineSegment(sketch, "E342", {"start": v(-53.37, 30.72) * mm, "end": v(-57.14, 33.9) * mm});
            skLineSegment(sketch, "E343", {"start": v(-57.14, 33.9) * mm, "end": v(-61.27, 37.8) * mm});
            skLineSegment(sketch, "E344", {"start": v(-61.27, 37.8) * mm, "end": v(-64.19, 40.73) * mm});
            skLineSegment(sketch, "E345", {"start": v(-64.19, 40.73) * mm, "end": v(-66.93, 43.6) * mm});
            skLineSegment(sketch, "E346", {"start": v(-66.93, 43.6) * mm, "end": v(-69.5, 46.4) * mm});
            skLineSegment(sketch, "E347", {"start": v(-69.5, 46.4) * mm, "end": v(-71.89, 49.11) * mm});
            skLineSegment(sketch, "E348", {"start": v(-71.89, 49.11) * mm, "end": v(-74.08, 51.75) * mm});
            skLineSegment(sketch, "E349", {"start": v(-74.08, 51.75) * mm, "end": v(-76.06, 54.3) * mm});
            skLineSegment(sketch, "E350", {"start": v(-76.06, 54.3) * mm, "end": v(-77.84, 56.77) * mm});
            skLineSegment(sketch, "E351", {"start": v(-77.84, 56.77) * mm, "end": v(-79.4, 59.14) * mm});
            skLineSegment(sketch, "E352", {"start": v(-79.4, 59.14) * mm, "end": v(-79.91, 60.34) * mm});
            skLineSegment(sketch, "E353", {"start": v(-79.91, 60.34) * mm, "end": v(-80, 61.55) * mm});
            skLineSegment(sketch, "E354", {"start": v(-80, 61.55) * mm, "end": v(-79.74, 62.7) * mm});
            skLineSegment(sketch, "E355", {"start": v(-79.74, 62.7) * mm, "end": v(-79.16, 63.7) * mm});
            skLineSegment(sketch, "E356", {"start": v(-79.16, 63.7) * mm, "end": v(-78.32, 64.51) * mm});
            skLineSegment(sketch, "E357", {"start": v(-78.32, 64.51) * mm, "end": v(-77.28, 65.05) * mm});
            skLineSegment(sketch, "E358", {"start": v(-77.28, 65.05) * mm, "end": v(-76.08, 65.25) * mm});
            skLineSegment(sketch, "E359", {"start": v(-76.08, 65.25) * mm, "end": v(-74.78, 65.05) * mm});
            skLineSegment(sketch, "E360", {"start": v(-74.78, 65.05) * mm, "end": v(-72.1, 64.13) * mm});
            skLineSegment(sketch, "E361", {"start": v(-72.1, 64.13) * mm, "end": v(-69.25, 63.02) * mm});
            skLineSegment(sketch, "E362", {"start": v(-69.25, 63.02) * mm, "end": v(-66.27, 61.74) * mm});
            skLineSegment(sketch, "E363", {"start": v(-66.27, 61.74) * mm, "end": v(-63.15, 60.28) * mm});
            skLineSegment(sketch, "E364", {"start": v(-63.15, 60.28) * mm, "end": v(-59.92, 58.63) * mm});
            skLineSegment(sketch, "E365", {"start": v(-59.92, 58.63) * mm, "end": v(-56.59, 56.8) * mm});
            skLineSegment(sketch, "E366", {"start": v(-56.59, 56.8) * mm, "end": v(-53.15, 54.8) * mm});
            skLineSegment(sketch, "E367", {"start": v(-53.15, 54.8) * mm, "end": v(-49.64, 52.6) * mm});
            skLineSegment(sketch, "E368", {"start": v(-49.64, 52.6) * mm, "end": v(-44.9, 49.36) * mm});
            skLineSegment(sketch, "E369", {"start": v(-44.9, 49.36) * mm, "end": v(-40.96, 46.3) * mm});
            skLineSegment(sketch, "E370", {"start": v(-40.96, 46.3) * mm, "end": v(-37.76, 43.37) * mm});
            skLineSegment(sketch, "E371", {"start": v(-37.76, 43.37) * mm, "end": v(-35.22, 40.56) * mm});
            skLineSegment(sketch, "E372", {"start": v(-35.22, 40.56) * mm, "end": v(-33.27, 37.83) * mm});
            skLineSegment(sketch, "E373", {"start": v(-33.27, 37.83) * mm, "end": v(-31.84, 35.15) * mm});
            skLineSegment(sketch, "E374", {"start": v(-31.84, 35.15) * mm, "end": v(-30.86, 32.5) * mm});
            skLineSegment(sketch, "E375", {"start": v(-30.86, 32.5) * mm, "end": v(-30.26, 29.84) * mm});
            skLineSegment(sketch, "E376", {"start": v(-30.26, 29.84) * mm, "end": v(-30.16, 29.12) * mm});
            skLineSegment(sketch, "E377", {"start": v(-30.16, 29.12) * mm, "end": v(-30.12, 28.45) * mm});
            skLineSegment(sketch, "E378", {"start": v(-30.12, 28.45) * mm, "end": v(-30.13, 27.82) * mm});
            skLineSegment(sketch, "E379", {"start": v(-30.13, 27.82) * mm, "end": v(-30.19, 27.23) * mm});
            skLineSegment(sketch, "E380", {"start": v(-30.19, 27.23) * mm, "end": v(-30.3, 26.69) * mm});
            skLineSegment(sketch, "E381", {"start": v(-30.3, 26.69) * mm, "end": v(-30.46, 26.2) * mm});
            skLineSegment(sketch, "E382", {"start": v(-30.46, 26.2) * mm, "end": v(-30.67, 25.76) * mm});
            skLineSegment(sketch, "E383", {"start": v(-30.67, 25.76) * mm, "end": v(-30.93, 25.37) * mm});
            skLineSegment(sketch, "E384", {"start": v(-138.72, 23.67) * mm, "end": v(-139.45, 23.73) * mm});
            skLineSegment(sketch, "E385", {"start": v(-139.45, 23.73) * mm, "end": v(-140.13, 23.84) * mm});
            skLineSegment(sketch, "E386", {"start": v(-140.13, 23.84) * mm, "end": v(-140.75, 23.99) * mm});
            skLineSegment(sketch, "E387", {"start": v(-140.75, 23.99) * mm, "end": v(-141.32, 24.18) * mm});
            skLineSegment(sketch, "E388", {"start": v(-141.32, 24.18) * mm, "end": v(-141.82, 24.4) * mm});
            skLineSegment(sketch, "E389", {"start": v(-141.82, 24.4) * mm, "end": v(-142.27, 24.67) * mm});
            skLineSegment(sketch, "E390", {"start": v(-142.27, 24.67) * mm, "end": v(-142.66, 24.98) * mm});
            skLineSegment(sketch, "E391", {"start": v(-142.66, 24.98) * mm, "end": v(-142.98, 25.32) * mm});
            skLineSegment(sketch, "E392", {"start": v(-142.98, 25.32) * mm, "end": v(-143.24, 25.7) * mm});
            skLineSegment(sketch, "E393", {"start": v(-143.24, 25.7) * mm, "end": v(-143.45, 26.14) * mm});
            skLineSegment(sketch, "E394", {"start": v(-143.45, 26.14) * mm, "end": v(-143.6, 26.63) * mm});
            skLineSegment(sketch, "E395", {"start": v(-143.6, 26.63) * mm, "end": v(-143.72, 27.17) * mm});
            skLineSegment(sketch, "E396", {"start": v(-143.72, 27.17) * mm, "end": v(-143.77, 27.75) * mm});
            skLineSegment(sketch, "E397", {"start": v(-143.77, 27.75) * mm, "end": v(-143.78, 28.38) * mm});
            skLineSegment(sketch, "E398", {"start": v(-143.78, 28.38) * mm, "end": v(-143.74, 29.04) * mm});
            skLineSegment(sketch, "E399", {"start": v(-143.74, 29.04) * mm, "end": v(-143.64, 29.75) * mm});
            skLineSegment(sketch, "E400", {"start": v(-143.64, 29.75) * mm, "end": v(-143, 32.4) * mm});
            skLineSegment(sketch, "E401", {"start": v(-143, 32.4) * mm, "end": v(-141.9, 35.08) * mm});
            skLineSegment(sketch, "E402", {"start": v(-141.9, 35.08) * mm, "end": v(-140.3, 37.8) * mm});
            skLineSegment(sketch, "E403", {"start": v(-140.3, 37.8) * mm, "end": v(-138.18, 40.59) * mm});
            skLineSegment(sketch, "E404", {"start": v(-138.18, 40.59) * mm, "end": v(-135.46, 43.46) * mm});
            skLineSegment(sketch, "E405", {"start": v(-135.46, 43.46) * mm, "end": v(-132.1, 46.42) * mm});
            skLineSegment(sketch, "E406", {"start": v(-132.1, 46.42) * mm, "end": v(-128.08, 49.5) * mm});
            skLineSegment(sketch, "E407", {"start": v(-128.08, 49.5) * mm, "end": v(-123.34, 52.73) * mm});
            skLineSegment(sketch, "E408", {"start": v(-123.34, 52.73) * mm, "end": v(-119.9, 54.88) * mm});
            skLineSegment(sketch, "E409", {"start": v(-119.9, 54.88) * mm, "end": v(-116.58, 56.84) * mm});
            skLineSegment(sketch, "E410", {"start": v(-116.58, 56.84) * mm, "end": v(-113.36, 58.6) * mm});
            skLineSegment(sketch, "E411", {"start": v(-113.36, 58.6) * mm, "end": v(-110.25, 60.19) * mm});
            skLineSegment(sketch, "E412", {"start": v(-110.25, 60.19) * mm, "end": v(-107.25, 61.6) * mm});
            skLineSegment(sketch, "E413", {"start": v(-107.25, 61.6) * mm, "end": v(-104.38, 62.82) * mm});
            skLineSegment(sketch, "E414", {"start": v(-104.38, 62.82) * mm, "end": v(-101.63, 63.89) * mm});
            skLineSegment(sketch, "E415", {"start": v(-101.63, 63.89) * mm, "end": v(-99.02, 64.79) * mm});
            skLineSegment(sketch, "E416", {"start": v(-99.02, 64.79) * mm, "end": v(-97.7, 65) * mm});
            skLineSegment(sketch, "E417", {"start": v(-97.7, 65) * mm, "end": v(-96.5, 64.8) * mm});
            skLineSegment(sketch, "E418", {"start": v(-96.5, 64.8) * mm, "end": v(-95.44, 64.25) * mm});
            skLineSegment(sketch, "E419", {"start": v(-95.44, 64.25) * mm, "end": v(-94.6, 63.43) * mm});
            skLineSegment(sketch, "E420", {"start": v(-94.6, 63.43) * mm, "end": v(-94.01, 62.4) * mm});
            skLineSegment(sketch, "E421", {"start": v(-94.01, 62.4) * mm, "end": v(-93.75, 61.25) * mm});
            skLineSegment(sketch, "E422", {"start": v(-93.75, 61.25) * mm, "end": v(-93.86, 60.03) * mm});
            skLineSegment(sketch, "E423", {"start": v(-93.86, 60.03) * mm, "end": v(-94.4, 58.82) * mm});
            skLineSegment(sketch, "E424", {"start": v(-94.4, 58.82) * mm, "end": v(-96.12, 56.28) * mm});
            skLineSegment(sketch, "E425", {"start": v(-96.12, 56.28) * mm, "end": v(-98.11, 53.6) * mm});
            skLineSegment(sketch, "E426", {"start": v(-98.11, 53.6) * mm, "end": v(-100.35, 50.78) * mm});
            skLineSegment(sketch, "E427", {"start": v(-100.35, 50.78) * mm, "end": v(-102.79, 47.87) * mm});
            skLineSegment(sketch, "E428", {"start": v(-102.79, 47.87) * mm, "end": v(-105.4, 44.9) * mm});
            skLineSegment(sketch, "E429", {"start": v(-105.4, 44.9) * mm, "end": v(-108.15, 41.9) * mm});
            skLineSegment(sketch, "E430", {"start": v(-108.15, 41.9) * mm, "end": v(-111.01, 38.91) * mm});
            skLineSegment(sketch, "E431", {"start": v(-111.01, 38.91) * mm, "end": v(-113.94, 35.96) * mm});
            skLineSegment(sketch, "E432", {"start": v(-113.94, 35.96) * mm, "end": v(-117.99, 32.17) * mm});
            skLineSegment(sketch, "E433", {"start": v(-117.99, 32.17) * mm, "end": v(-121.6, 29.21) * mm});
            skLineSegment(sketch, "E434", {"start": v(-121.6, 29.21) * mm, "end": v(-124.88, 27) * mm});
            skLineSegment(sketch, "E435", {"start": v(-124.88, 27) * mm, "end": v(-127.88, 25.42) * mm});
            skLineSegment(sketch, "E436", {"start": v(-127.88, 25.42) * mm, "end": v(-130.69, 24.39) * mm});
            skLineSegment(sketch, "E437", {"start": v(-130.69, 24.39) * mm, "end": v(-133.38, 23.82) * mm});
            skLineSegment(sketch, "E438", {"start": v(-133.38, 23.82) * mm, "end": v(-136.03, 23.6) * mm});
            skLineSegment(sketch, "E439", {"start": v(-136.03, 23.6) * mm, "end": v(-138.72, 23.67) * mm});
            skLineSegment(sketch, "E440", {"start": v(-130.05, 62.51) * mm, "end": v(-134.43, 62.2) * mm});
            skLineSegment(sketch, "E441", {"start": v(-134.43, 62.2) * mm, "end": v(-138.81, 62.17) * mm});
            skLineSegment(sketch, "E442", {"start": v(-138.81, 62.17) * mm, "end": v(-143.1, 62.41) * mm});
            skLineSegment(sketch, "E443", {"start": v(-143.1, 62.41) * mm, "end": v(-147.18, 62.93) * mm});
            skLineSegment(sketch, "E444", {"start": v(-147.18, 62.93) * mm, "end": v(-150.97, 63.73) * mm});
            skLineSegment(sketch, "E445", {"start": v(-150.97, 63.73) * mm, "end": v(-154.38, 64.8) * mm});
            skLineSegment(sketch, "E446", {"start": v(-154.38, 64.8) * mm, "end": v(-157.3, 66.18) * mm});
            skLineSegment(sketch, "E447", {"start": v(-157.3, 66.18) * mm, "end": v(-159.65, 67.85) * mm});
            skLineSegment(sketch, "E448", {"start": v(-159.65, 67.85) * mm, "end": v(-160.17, 68.35) * mm});
            skLineSegment(sketch, "E449", {"start": v(-160.17, 68.35) * mm, "end": v(-160.64, 68.86) * mm});
            skLineSegment(sketch, "E450", {"start": v(-160.64, 68.86) * mm, "end": v(-161.03, 69.36) * mm});
            skLineSegment(sketch, "E451", {"start": v(-161.03, 69.36) * mm, "end": v(-161.35, 69.86) * mm});
            skLineSegment(sketch, "E452", {"start": v(-161.35, 69.86) * mm, "end": v(-161.6, 70.35) * mm});
            skLineSegment(sketch, "E453", {"start": v(-161.6, 70.35) * mm, "end": v(-161.79, 70.84) * mm});
            skLineSegment(sketch, "E454", {"start": v(-161.79, 70.84) * mm, "end": v(-161.9, 71.31) * mm});
            skLineSegment(sketch, "E455", {"start": v(-161.9, 71.31) * mm, "end": v(-161.94, 71.78) * mm});
            skLineSegment(sketch, "E456", {"start": v(-161.94, 71.78) * mm, "end": v(-161.9, 72.24) * mm});
            skLineSegment(sketch, "E457", {"start": v(-161.9, 72.24) * mm, "end": v(-161.8, 72.7) * mm});
            skLineSegment(sketch, "E458", {"start": v(-161.8, 72.7) * mm, "end": v(-161.62, 73.19) * mm});
            skLineSegment(sketch, "E459", {"start": v(-161.62, 73.19) * mm, "end": v(-161.37, 73.67) * mm});
            skLineSegment(sketch, "E460", {"start": v(-161.37, 73.67) * mm, "end": v(-161.06, 74.16) * mm});
            skLineSegment(sketch, "E461", {"start": v(-161.06, 74.16) * mm, "end": v(-160.67, 74.65) * mm});
            skLineSegment(sketch, "E462", {"start": v(-160.67, 74.65) * mm, "end": v(-160.23, 75.15) * mm});
            skLineSegment(sketch, "E463", {"start": v(-160.23, 75.15) * mm, "end": v(-159.71, 75.64) * mm});
            skLineSegment(sketch, "E464", {"start": v(-159.71, 75.64) * mm, "end": v(-157.87, 77.06) * mm});
            skLineSegment(sketch, "E465", {"start": v(-157.87, 77.06) * mm, "end": v(-155.7, 78.26) * mm});
            skLineSegment(sketch, "E466", {"start": v(-155.7, 78.26) * mm, "end": v(-153.23, 79.27) * mm});
            skLineSegment(sketch, "E467", {"start": v(-153.23, 79.27) * mm, "end": v(-150.49, 80.07) * mm});
            skLineSegment(sketch, "E468", {"start": v(-150.49, 80.07) * mm, "end": v(-147.5, 80.69) * mm});
            skLineSegment(sketch, "E469", {"start": v(-147.5, 80.69) * mm, "end": v(-144.27, 81.1) * mm});
            skLineSegment(sketch, "E470", {"start": v(-144.27, 81.1) * mm, "end": v(-140.84, 81.35) * mm});
            skLineSegment(sketch, "E471", {"start": v(-140.84, 81.35) * mm, "end": v(-137.23, 81.4) * mm});
            skLineSegment(sketch, "E472", {"start": v(-137.23, 81.4) * mm, "end": v(-136.35, 81.39) * mm});
            skLineSegment(sketch, "E473", {"start": v(-136.35, 81.39) * mm, "end": v(-135.47, 81.37) * mm});
            skLineSegment(sketch, "E474", {"start": v(-135.47, 81.37) * mm, "end": v(-134.58, 81.34) * mm});
            skLineSegment(sketch, "E475", {"start": v(-134.58, 81.34) * mm, "end": v(-133.68, 81.3) * mm});
            skLineSegment(sketch, "E476", {"start": v(-133.68, 81.3) * mm, "end": v(-132.78, 81.25) * mm});
            skLineSegment(sketch, "E477", {"start": v(-132.78, 81.25) * mm, "end": v(-131.87, 81.2) * mm});
            skLineSegment(sketch, "E478", {"start": v(-131.87, 81.2) * mm, "end": v(-130.96, 81.12) * mm});
            skLineSegment(sketch, "E479", {"start": v(-130.96, 81.12) * mm, "end": v(-130.04, 81.04) * mm});
            skLineSegment(sketch, "E480", {"start": v(-130.04, 81.04) * mm, "end": v(-125.1, 80.46) * mm});
            skLineSegment(sketch, "E481", {"start": v(-125.1, 80.46) * mm, "end": v(-120.36, 79.73) * mm});
            skLineSegment(sketch, "E482", {"start": v(-120.36, 79.73) * mm, "end": v(-115.82, 78.87) * mm});
            skLineSegment(sketch, "E483", {"start": v(-115.82, 78.87) * mm, "end": v(-111.56, 77.92) * mm});
            skLineSegment(sketch, "E484", {"start": v(-111.56, 77.92) * mm, "end": v(-107.6, 76.91) * mm});
            skLineSegment(sketch, "E485", {"start": v(-107.6, 76.91) * mm, "end": v(-103.99, 75.87) * mm});
            skLineSegment(sketch, "E486", {"start": v(-103.99, 75.87) * mm, "end": v(-100.77, 74.82) * mm});
            skLineSegment(sketch, "E487", {"start": v(-100.77, 74.82) * mm, "end": v(-97.99, 73.79) * mm});
            skLineSegment(sketch, "E488", {"start": v(-97.99, 73.79) * mm, "end": v(-97.4, 73.44) * mm});
            skLineSegment(sketch, "E489", {"start": v(-97.4, 73.44) * mm, "end": v(-96.97, 72.96) * mm});
            skLineSegment(sketch, "E490", {"start": v(-96.97, 72.96) * mm, "end": v(-96.71, 72.4) * mm});
            skLineSegment(sketch, "E491", {"start": v(-96.71, 72.4) * mm, "end": v(-96.63, 71.8) * mm});
            skLineSegment(sketch, "E492", {"start": v(-96.63, 71.8) * mm, "end": v(-96.71, 71.19) * mm});
            skLineSegment(sketch, "E493", {"start": v(-96.71, 71.19) * mm, "end": v(-96.97, 70.63) * mm});
            skLineSegment(sketch, "E494", {"start": v(-96.97, 70.63) * mm, "end": v(-97.4, 70.15) * mm});
            skLineSegment(sketch, "E495", {"start": v(-97.4, 70.15) * mm, "end": v(-98, 69.8) * mm});
            skLineSegment(sketch, "E496", {"start": v(-98, 69.8) * mm, "end": v(-100.78, 68.8) * mm});
            skLineSegment(sketch, "E497", {"start": v(-100.78, 68.8) * mm, "end": v(-104, 67.76) * mm});
            skLineSegment(sketch, "E498", {"start": v(-104, 67.76) * mm, "end": v(-107.6, 66.72) * mm});
            skLineSegment(sketch, "E499", {"start": v(-107.6, 66.72) * mm, "end": v(-111.57, 65.71) * mm});
            skLineSegment(sketch, "E500", {"start": v(-111.57, 65.71) * mm, "end": v(-115.84, 64.76) * mm});
            skLineSegment(sketch, "E501", {"start": v(-115.84, 64.76) * mm, "end": v(-120.37, 63.9) * mm});
            skLineSegment(sketch, "E502", {"start": v(-120.37, 63.9) * mm, "end": v(-125.12, 63.13) * mm});
            skLineSegment(sketch, "E503", {"start": v(-125.12, 63.13) * mm, "end": v(-130.05, 62.51) * mm});
            skSolve(sketch);
        }
        {
            var Q0;
            Q0=makeQuery(id+"F0.imprint","IMPRINT",FACE,{"disambiguationData":[TD([[makeQuery(id+"F0.imprint","IMPRINT",EDGE,{"derivedFrom":sQuery(id+"F0.wireOp",EDGE,"E0")}),1.0]])]});
            extrude(context, id + "F1", {"entities" : qUnion([Q0]), "depth" : 12 * mm});
        }
        {
            var Q0;
            Q0=makeQuery(id+"F1.opExtrude","SWEPT_BODY",BODY,{"disambiguationData":[OSD([sQuery(id+"F0.wireOp",EDGE,"E0"),sQuery(id+"F0.wireOp",EDGE,"E1"),sQuery(id+"F0.wireOp",EDGE,"E2"),sQuery(id+"F0.wireOp",EDGE,"E3"),sQuery(id+"F0.wireOp",EDGE,"E4"),sQuery(id+"F0.wireOp",EDGE,"E5"),sQuery(id+"F0.wireOp",EDGE,"E6"),sQuery(id+"F0.wireOp",EDGE,"E7"),sQuery(id+"F0.wireOp",EDGE,"E8"),sQuery(id+"F0.wireOp",EDGE,"E9"),sQuery(id+"F0.wireOp",EDGE,"E10"),sQuery(id+"F0.wireOp",EDGE,"E11"),sQuery(id+"F0.wireOp",EDGE,"E12"),sQuery(id+"F0.wireOp",EDGE,"E13"),sQuery(id+"F0.wireOp",EDGE,"E14"),sQuery(id+"F0.wireOp",EDGE,"E15"),sQuery(id+"F0.wireOp",EDGE,"E16"),sQuery(id+"F0.wireOp",EDGE,"E17"),sQuery(id+"F0.wireOp",EDGE,"E18"),sQuery(id+"F0.wireOp",EDGE,"E19"),sQuery(id+"F0.wireOp",EDGE,"E20"),sQuery(id+"F0.wireOp",EDGE,"E21"),sQuery(id+"F0.wireOp",EDGE,"E22"),sQuery(id+"F0.wireOp",EDGE,"E23"),sQuery(id+"F0.wireOp",EDGE,"E24"),sQuery(id+"F0.wireOp",EDGE,"E25"),sQuery(id+"F0.wireOp",EDGE,"E26"),sQuery(id+"F0.wireOp",EDGE,"E27"),sQuery(id+"F0.wireOp",EDGE,"E28"),sQuery(id+"F0.wireOp",EDGE,"E29"),sQuery(id+"F0.wireOp",EDGE,"E30"),sQuery(id+"F0.wireOp",EDGE,"E31"),sQuery(id+"F0.wireOp",EDGE,"E32"),sQuery(id+"F0.wireOp",EDGE,"E33"),sQuery(id+"F0.wireOp",EDGE,"E34"),sQuery(id+"F0.wireOp",EDGE,"E35"),sQuery(id+"F0.wireOp",EDGE,"E36"),sQuery(id+"F0.wireOp",EDGE,"E37"),sQuery(id+"F0.wireOp",EDGE,"E38"),sQuery(id+"F0.wireOp",EDGE,"E39"),sQuery(id+"F0.wireOp",EDGE,"E40"),sQuery(id+"F0.wireOp",EDGE,"E41"),sQuery(id+"F0.wireOp",EDGE,"E42"),sQuery(id+"F0.wireOp",EDGE,"E43"),sQuery(id+"F0.wireOp",EDGE,"E44"),sQuery(id+"F0.wireOp",EDGE,"E45"),sQuery(id+"F0.wireOp",EDGE,"E46"),sQuery(id+"F0.wireOp",EDGE,"E47"),sQuery(id+"F0.wireOp",EDGE,"E48"),sQuery(id+"F0.wireOp",EDGE,"E49"),sQuery(id+"F0.wireOp",EDGE,"E50"),sQuery(id+"F0.wireOp",EDGE,"E51"),sQuery(id+"F0.wireOp",EDGE,"E52"),sQuery(id+"F0.wireOp",EDGE,"E53"),sQuery(id+"F0.wireOp",EDGE,"E54"),sQuery(id+"F0.wireOp",EDGE,"E55"),sQuery(id+"F0.wireOp",EDGE,"E56"),sQuery(id+"F0.wireOp",EDGE,"E57"),sQuery(id+"F0.wireOp",EDGE,"E58"),sQuery(id+"F0.wireOp",EDGE,"E59"),sQuery(id+"F0.wireOp",EDGE,"E60"),sQuery(id+"F0.wireOp",EDGE,"E61"),sQuery(id+"F0.wireOp",EDGE,"E62"),sQuery(id+"F0.wireOp",EDGE,"E63"),sQuery(id+"F0.wireOp",EDGE,"E64"),sQuery(id+"F0.wireOp",EDGE,"E65"),sQuery(id+"F0.wireOp",EDGE,"E66"),sQuery(id+"F0.wireOp",EDGE,"E67"),sQuery(id+"F0.wireOp",EDGE,"E68"),sQuery(id+"F0.wireOp",EDGE,"E69"),sQuery(id+"F0.wireOp",EDGE,"E70"),sQuery(id+"F0.wireOp",EDGE,"E71"),sQuery(id+"F0.wireOp",EDGE,"E72"),sQuery(id+"F0.wireOp",EDGE,"E73"),sQuery(id+"F0.wireOp",EDGE,"E74"),sQuery(id+"F0.wireOp",EDGE,"E75"),sQuery(id+"F0.wireOp",EDGE,"E76"),sQuery(id+"F0.wireOp",EDGE,"E77"),sQuery(id+"F0.wireOp",EDGE,"E78"),sQuery(id+"F0.wireOp",EDGE,"E79"),sQuery(id+"F0.wireOp",EDGE,"E80"),sQuery(id+"F0.wireOp",EDGE,"E81"),sQuery(id+"F0.wireOp",EDGE,"E82"),sQuery(id+"F0.wireOp",EDGE,"E83"),sQuery(id+"F0.wireOp",EDGE,"E84"),sQuery(id+"F0.wireOp",EDGE,"E85"),sQuery(id+"F0.wireOp",EDGE,"E86"),sQuery(id+"F0.wireOp",EDGE,"E87"),sQuery(id+"F0.wireOp",EDGE,"E88"),sQuery(id+"F0.wireOp",EDGE,"E89"),sQuery(id+"F0.wireOp",EDGE,"E90"),sQuery(id+"F0.wireOp",EDGE,"E91"),sQuery(id+"F0.wireOp",EDGE,"E92"),sQuery(id+"F0.wireOp",EDGE,"E93"),sQuery(id+"F0.wireOp",EDGE,"E94"),sQuery(id+"F0.wireOp",EDGE,"E95"),sQuery(id+"F0.wireOp",EDGE,"E96"),sQuery(id+"F0.wireOp",EDGE,"E97"),sQuery(id+"F0.wireOp",EDGE,"E98"),sQuery(id+"F0.wireOp",EDGE,"E99"),sQuery(id+"F0.wireOp",EDGE,"E100"),sQuery(id+"F0.wireOp",EDGE,"E101"),sQuery(id+"F0.wireOp",EDGE,"E102"),sQuery(id+"F0.wireOp",EDGE,"E103"),sQuery(id+"F0.wireOp",EDGE,"E104"),sQuery(id+"F0.wireOp",EDGE,"E105"),sQuery(id+"F0.wireOp",EDGE,"E106"),sQuery(id+"F0.wireOp",EDGE,"E107"),sQuery(id+"F0.wireOp",EDGE,"E108"),sQuery(id+"F0.wireOp",EDGE,"E109"),sQuery(id+"F0.wireOp",EDGE,"E110"),sQuery(id+"F0.wireOp",EDGE,"E111"),sQuery(id+"F0.wireOp",EDGE,"E112"),sQuery(id+"F0.wireOp",EDGE,"E113"),sQuery(id+"F0.wireOp",EDGE,"E114"),sQuery(id+"F0.wireOp",EDGE,"E115"),sQuery(id+"F0.wireOp",EDGE,"E116"),sQuery(id+"F0.wireOp",EDGE,"E117"),sQuery(id+"F0.wireOp",EDGE,"E118"),sQuery(id+"F0.wireOp",EDGE,"E119"),sQuery(id+"F0.wireOp",EDGE,"E120"),sQuery(id+"F0.wireOp",EDGE,"E121"),sQuery(id+"F0.wireOp",EDGE,"E122"),sQuery(id+"F0.wireOp",EDGE,"E123"),sQuery(id+"F0.wireOp",EDGE,"E124"),sQuery(id+"F0.wireOp",EDGE,"E125"),sQuery(id+"F0.wireOp",EDGE,"E126"),sQuery(id+"F0.wireOp",EDGE,"E127"),sQuery(id+"F0.wireOp",EDGE,"E128"),sQuery(id+"F0.wireOp",EDGE,"E129"),sQuery(id+"F0.wireOp",EDGE,"E130"),sQuery(id+"F0.wireOp",EDGE,"E131"),sQuery(id+"F0.wireOp",EDGE,"E132"),sQuery(id+"F0.wireOp",EDGE,"E133"),sQuery(id+"F0.wireOp",EDGE,"E134"),sQuery(id+"F0.wireOp",EDGE,"E135"),sQuery(id+"F0.wireOp",EDGE,"E136"),sQuery(id+"F0.wireOp",EDGE,"E137"),sQuery(id+"F0.wireOp",EDGE,"E138"),sQuery(id+"F0.wireOp",EDGE,"E139"),sQuery(id+"F0.wireOp",EDGE,"E140"),sQuery(id+"F0.wireOp",EDGE,"E141"),sQuery(id+"F0.wireOp",EDGE,"E142"),sQuery(id+"F0.wireOp",EDGE,"E143"),sQuery(id+"F0.wireOp",EDGE,"E144"),sQuery(id+"F0.wireOp",EDGE,"E145"),sQuery(id+"F0.wireOp",EDGE,"E146"),sQuery(id+"F0.wireOp",EDGE,"E147"),sQuery(id+"F0.wireOp",EDGE,"E148"),sQuery(id+"F0.wireOp",EDGE,"E149"),sQuery(id+"F0.wireOp",EDGE,"E150"),sQuery(id+"F0.wireOp",EDGE,"E151"),sQuery(id+"F0.wireOp",EDGE,"E152"),sQuery(id+"F0.wireOp",EDGE,"E153"),sQuery(id+"F0.wireOp",EDGE,"E154"),sQuery(id+"F0.wireOp",EDGE,"E155"),sQuery(id+"F0.wireOp",EDGE,"E156"),sQuery(id+"F0.wireOp",EDGE,"E157"),sQuery(id+"F0.wireOp",EDGE,"E158"),sQuery(id+"F0.wireOp",EDGE,"E159"),sQuery(id+"F0.wireOp",EDGE,"E160"),sQuery(id+"F0.wireOp",EDGE,"E161"),sQuery(id+"F0.wireOp",EDGE,"E162"),sQuery(id+"F0.wireOp",EDGE,"E163"),sQuery(id+"F0.wireOp",EDGE,"E164"),sQuery(id+"F0.wireOp",EDGE,"E165"),sQuery(id+"F0.wireOp",EDGE,"E166"),sQuery(id+"F0.wireOp",EDGE,"E167"),sQuery(id+"F0.wireOp",EDGE,"E168"),sQuery(id+"F0.wireOp",EDGE,"E169"),sQuery(id+"F0.wireOp",EDGE,"E170"),sQuery(id+"F0.wireOp",EDGE,"E171"),sQuery(id+"F0.wireOp",EDGE,"E172"),sQuery(id+"F0.wireOp",EDGE,"E173"),sQuery(id+"F0.wireOp",EDGE,"E174"),sQuery(id+"F0.wireOp",EDGE,"E175"),sQuery(id+"F0.wireOp",EDGE,"E176"),sQuery(id+"F0.wireOp",EDGE,"E177"),sQuery(id+"F0.wireOp",EDGE,"E178"),sQuery(id+"F0.wireOp",EDGE,"E179"),sQuery(id+"F0.wireOp",EDGE,"E180"),sQuery(id+"F0.wireOp",EDGE,"E181"),sQuery(id+"F0.wireOp",EDGE,"E182"),sQuery(id+"F0.wireOp",EDGE,"E183"),sQuery(id+"F0.wireOp",EDGE,"E184"),sQuery(id+"F0.wireOp",EDGE,"E185"),sQuery(id+"F0.wireOp",EDGE,"E186"),sQuery(id+"F0.wireOp",EDGE,"E187"),sQuery(id+"F0.wireOp",EDGE,"E188"),sQuery(id+"F0.wireOp",EDGE,"E189"),sQuery(id+"F0.wireOp",EDGE,"E190"),sQuery(id+"F0.wireOp",EDGE,"E191"),sQuery(id+"F0.wireOp",EDGE,"E192"),sQuery(id+"F0.wireOp",EDGE,"E193"),sQuery(id+"F0.wireOp",EDGE,"E194"),sQuery(id+"F0.wireOp",EDGE,"E195"),sQuery(id+"F0.wireOp",EDGE,"E196"),sQuery(id+"F0.wireOp",EDGE,"E197"),sQuery(id+"F0.wireOp",EDGE,"E198"),sQuery(id+"F0.wireOp",EDGE,"E199"),sQuery(id+"F0.wireOp",EDGE,"E200"),sQuery(id+"F0.wireOp",EDGE,"E201"),sQuery(id+"F0.wireOp",EDGE,"E202"),sQuery(id+"F0.wireOp",EDGE,"E203"),sQuery(id+"F0.wireOp",EDGE,"E204"),sQuery(id+"F0.wireOp",EDGE,"E205"),sQuery(id+"F0.wireOp",EDGE,"E206"),sQuery(id+"F0.wireOp",EDGE,"E207"),sQuery(id+"F0.wireOp",EDGE,"E208"),sQuery(id+"F0.wireOp",EDGE,"E209"),sQuery(id+"F0.wireOp",EDGE,"E210"),sQuery(id+"F0.wireOp",EDGE,"E211"),sQuery(id+"F0.wireOp",EDGE,"E212"),sQuery(id+"F0.wireOp",EDGE,"E213"),sQuery(id+"F0.wireOp",EDGE,"E214"),sQuery(id+"F0.wireOp",EDGE,"E215"),sQuery(id+"F0.wireOp",EDGE,"E216"),sQuery(id+"F0.wireOp",EDGE,"E217"),sQuery(id+"F0.wireOp",EDGE,"E218"),sQuery(id+"F0.wireOp",EDGE,"E219"),sQuery(id+"F0.wireOp",EDGE,"E220"),sQuery(id+"F0.wireOp",EDGE,"E221"),sQuery(id+"F0.wireOp",EDGE,"E222"),sQuery(id+"F0.wireOp",EDGE,"E223"),sQuery(id+"F0.wireOp",EDGE,"E224"),sQuery(id+"F0.wireOp",EDGE,"E225"),sQuery(id+"F0.wireOp",EDGE,"E226"),sQuery(id+"F0.wireOp",EDGE,"E227"),sQuery(id+"F0.wireOp",EDGE,"E228"),sQuery(id+"F0.wireOp",EDGE,"E229"),sQuery(id+"F0.wireOp",EDGE,"E230"),sQuery(id+"F0.wireOp",EDGE,"E231"),sQuery(id+"F0.wireOp",EDGE,"E232"),sQuery(id+"F0.wireOp",EDGE,"E233"),sQuery(id+"F0.wireOp",EDGE,"E234"),sQuery(id+"F0.wireOp",EDGE,"E235"),sQuery(id+"F0.wireOp",EDGE,"E236"),sQuery(id+"F0.wireOp",EDGE,"E237"),sQuery(id+"F0.wireOp",EDGE,"E238"),sQuery(id+"F0.wireOp",EDGE,"E239"),sQuery(id+"F0.wireOp",EDGE,"E240"),sQuery(id+"F0.wireOp",EDGE,"E241"),sQuery(id+"F0.wireOp",EDGE,"E242"),sQuery(id+"F0.wireOp",EDGE,"E243"),sQuery(id+"F0.wireOp",EDGE,"E244"),sQuery(id+"F0.wireOp",EDGE,"E245"),sQuery(id+"F0.wireOp",EDGE,"E246"),sQuery(id+"F0.wireOp",EDGE,"E247"),sQuery(id+"F0.wireOp",EDGE,"E248"),sQuery(id+"F0.wireOp",EDGE,"E249"),sQuery(id+"F0.wireOp",EDGE,"E250"),sQuery(id+"F0.wireOp",EDGE,"E251"),sQuery(id+"F0.wireOp",EDGE,"E252"),sQuery(id+"F0.wireOp",EDGE,"E253"),sQuery(id+"F0.wireOp",EDGE,"E254"),sQuery(id+"F0.wireOp",EDGE,"E255"),sQuery(id+"F0.wireOp",EDGE,"E256"),sQuery(id+"F0.wireOp",EDGE,"E257"),sQuery(id+"F0.wireOp",EDGE,"E258"),sQuery(id+"F0.wireOp",EDGE,"E259"),sQuery(id+"F0.wireOp",EDGE,"E260"),sQuery(id+"F0.wireOp",EDGE,"E261"),sQuery(id+"F0.wireOp",EDGE,"E262"),sQuery(id+"F0.wireOp",EDGE,"E263"),sQuery(id+"F0.wireOp",EDGE,"E264"),sQuery(id+"F0.wireOp",EDGE,"E265"),sQuery(id+"F0.wireOp",EDGE,"E266"),sQuery(id+"F0.wireOp",EDGE,"E267"),sQuery(id+"F0.wireOp",EDGE,"E268"),sQuery(id+"F0.wireOp",EDGE,"E269"),sQuery(id+"F0.wireOp",EDGE,"E270"),sQuery(id+"F0.wireOp",EDGE,"E271"),sQuery(id+"F0.wireOp",EDGE,"E272"),sQuery(id+"F0.wireOp",EDGE,"E273"),sQuery(id+"F0.wireOp",EDGE,"E274"),sQuery(id+"F0.wireOp",EDGE,"E275"),sQuery(id+"F0.wireOp",EDGE,"E276"),sQuery(id+"F0.wireOp",EDGE,"E277"),sQuery(id+"F0.wireOp",EDGE,"E278"),sQuery(id+"F0.wireOp",EDGE,"E279"),sQuery(id+"F0.wireOp",EDGE,"E280"),sQuery(id+"F0.wireOp",EDGE,"E281"),sQuery(id+"F0.wireOp",EDGE,"E282"),sQuery(id+"F0.wireOp",EDGE,"E283"),sQuery(id+"F0.wireOp",EDGE,"E284"),sQuery(id+"F0.wireOp",EDGE,"E285"),sQuery(id+"F0.wireOp",EDGE,"E286"),sQuery(id+"F0.wireOp",EDGE,"E287"),sQuery(id+"F0.wireOp",EDGE,"E288"),sQuery(id+"F0.wireOp",EDGE,"E289"),sQuery(id+"F0.wireOp",EDGE,"E290"),sQuery(id+"F0.wireOp",EDGE,"E291"),sQuery(id+"F0.wireOp",EDGE,"E292"),sQuery(id+"F0.wireOp",EDGE,"E293"),sQuery(id+"F0.wireOp",EDGE,"E294"),sQuery(id+"F0.wireOp",EDGE,"E295"),sQuery(id+"F0.wireOp",EDGE,"E296"),sQuery(id+"F0.wireOp",EDGE,"E297"),sQuery(id+"F0.wireOp",EDGE,"E298"),sQuery(id+"F0.wireOp",EDGE,"E299"),sQuery(id+"F0.wireOp",EDGE,"E300"),sQuery(id+"F0.wireOp",EDGE,"E301"),sQuery(id+"F0.wireOp",EDGE,"E302"),sQuery(id+"F0.wireOp",EDGE,"E303"),sQuery(id+"F0.wireOp",EDGE,"E304"),sQuery(id+"F0.wireOp",EDGE,"E305"),sQuery(id+"F0.wireOp",EDGE,"E306"),sQuery(id+"F0.wireOp",EDGE,"E307"),sQuery(id+"F0.wireOp",EDGE,"E308"),sQuery(id+"F0.wireOp",EDGE,"E309"),sQuery(id+"F0.wireOp",EDGE,"E310"),sQuery(id+"F0.wireOp",EDGE,"E311"),sQuery(id+"F0.wireOp",EDGE,"E312"),sQuery(id+"F0.wireOp",EDGE,"E313"),sQuery(id+"F0.wireOp",EDGE,"E314"),sQuery(id+"F0.wireOp",EDGE,"E315"),sQuery(id+"F0.wireOp",EDGE,"E316"),sQuery(id+"F0.wireOp",EDGE,"E317"),sQuery(id+"F0.wireOp",EDGE,"E318"),sQuery(id+"F0.wireOp",EDGE,"E319"),sQuery(id+"F0.wireOp",EDGE,"E320"),sQuery(id+"F0.wireOp",EDGE,"E321"),sQuery(id+"F0.wireOp",EDGE,"E322"),sQuery(id+"F0.wireOp",EDGE,"E323"),sQuery(id+"F0.wireOp",EDGE,"E324"),sQuery(id+"F0.wireOp",EDGE,"E325"),sQuery(id+"F0.wireOp",EDGE,"E326"),sQuery(id+"F0.wireOp",EDGE,"E327"),sQuery(id+"F0.wireOp",EDGE,"E328"),sQuery(id+"F0.wireOp",EDGE,"E329"),sQuery(id+"F0.wireOp",EDGE,"E330"),sQuery(id+"F0.wireOp",EDGE,"E331"),sQuery(id+"F0.wireOp",EDGE,"E332"),sQuery(id+"F0.wireOp",EDGE,"E333"),sQuery(id+"F0.wireOp",EDGE,"E334"),sQuery(id+"F0.wireOp",EDGE,"E335"),sQuery(id+"F0.wireOp",EDGE,"E336"),sQuery(id+"F0.wireOp",EDGE,"E337"),sQuery(id+"F0.wireOp",EDGE,"E338"),sQuery(id+"F0.wireOp",EDGE,"E339"),sQuery(id+"F0.wireOp",EDGE,"E340"),sQuery(id+"F0.wireOp",EDGE,"E341"),sQuery(id+"F0.wireOp",EDGE,"E342"),sQuery(id+"F0.wireOp",EDGE,"E343"),sQuery(id+"F0.wireOp",EDGE,"E344"),sQuery(id+"F0.wireOp",EDGE,"E345"),sQuery(id+"F0.wireOp",EDGE,"E346"),sQuery(id+"F0.wireOp",EDGE,"E347"),sQuery(id+"F0.wireOp",EDGE,"E348"),sQuery(id+"F0.wireOp",EDGE,"E349"),sQuery(id+"F0.wireOp",EDGE,"E350"),sQuery(id+"F0.wireOp",EDGE,"E351"),sQuery(id+"F0.wireOp",EDGE,"E352"),sQuery(id+"F0.wireOp",EDGE,"E353"),sQuery(id+"F0.wireOp",EDGE,"E354"),sQuery(id+"F0.wireOp",EDGE,"E355"),sQuery(id+"F0.wireOp",EDGE,"E356"),sQuery(id+"F0.wireOp",EDGE,"E357"),sQuery(id+"F0.wireOp",EDGE,"E358"),sQuery(id+"F0.wireOp",EDGE,"E359"),sQuery(id+"F0.wireOp",EDGE,"E360"),sQuery(id+"F0.wireOp",EDGE,"E361"),sQuery(id+"F0.wireOp",EDGE,"E362"),sQuery(id+"F0.wireOp",EDGE,"E363"),sQuery(id+"F0.wireOp",EDGE,"E364"),sQuery(id+"F0.wireOp",EDGE,"E365"),sQuery(id+"F0.wireOp",EDGE,"E366"),sQuery(id+"F0.wireOp",EDGE,"E367"),sQuery(id+"F0.wireOp",EDGE,"E368"),sQuery(id+"F0.wireOp",EDGE,"E369"),sQuery(id+"F0.wireOp",EDGE,"E370"),sQuery(id+"F0.wireOp",EDGE,"E371"),sQuery(id+"F0.wireOp",EDGE,"E372"),sQuery(id+"F0.wireOp",EDGE,"E373"),sQuery(id+"F0.wireOp",EDGE,"E374"),sQuery(id+"F0.wireOp",EDGE,"E375"),sQuery(id+"F0.wireOp",EDGE,"E376"),sQuery(id+"F0.wireOp",EDGE,"E377"),sQuery(id+"F0.wireOp",EDGE,"E378"),sQuery(id+"F0.wireOp",EDGE,"E379"),sQuery(id+"F0.wireOp",EDGE,"E380"),sQuery(id+"F0.wireOp",EDGE,"E381"),sQuery(id+"F0.wireOp",EDGE,"E382"),sQuery(id+"F0.wireOp",EDGE,"E383"),sQuery(id+"F0.wireOp",EDGE,"E384"),sQuery(id+"F0.wireOp",EDGE,"E385"),sQuery(id+"F0.wireOp",EDGE,"E386"),sQuery(id+"F0.wireOp",EDGE,"E387"),sQuery(id+"F0.wireOp",EDGE,"E388"),sQuery(id+"F0.wireOp",EDGE,"E389"),sQuery(id+"F0.wireOp",EDGE,"E390"),sQuery(id+"F0.wireOp",EDGE,"E391"),sQuery(id+"F0.wireOp",EDGE,"E392"),sQuery(id+"F0.wireOp",EDGE,"E393"),sQuery(id+"F0.wireOp",EDGE,"E394"),sQuery(id+"F0.wireOp",EDGE,"E395"),sQuery(id+"F0.wireOp",EDGE,"E396"),sQuery(id+"F0.wireOp",EDGE,"E397"),sQuery(id+"F0.wireOp",EDGE,"E398"),sQuery(id+"F0.wireOp",EDGE,"E399"),sQuery(id+"F0.wireOp",EDGE,"E400"),sQuery(id+"F0.wireOp",EDGE,"E401"),sQuery(id+"F0.wireOp",EDGE,"E402"),sQuery(id+"F0.wireOp",EDGE,"E403"),sQuery(id+"F0.wireOp",EDGE,"E404"),sQuery(id+"F0.wireOp",EDGE,"E405"),sQuery(id+"F0.wireOp",EDGE,"E406"),sQuery(id+"F0.wireOp",EDGE,"E407"),sQuery(id+"F0.wireOp",EDGE,"E408"),sQuery(id+"F0.wireOp",EDGE,"E409"),sQuery(id+"F0.wireOp",EDGE,"E410"),sQuery(id+"F0.wireOp",EDGE,"E411"),sQuery(id+"F0.wireOp",EDGE,"E412"),sQuery(id+"F0.wireOp",EDGE,"E413"),sQuery(id+"F0.wireOp",EDGE,"E414"),sQuery(id+"F0.wireOp",EDGE,"E415"),sQuery(id+"F0.wireOp",EDGE,"E416"),sQuery(id+"F0.wireOp",EDGE,"E417"),sQuery(id+"F0.wireOp",EDGE,"E418"),sQuery(id+"F0.wireOp",EDGE,"E419"),sQuery(id+"F0.wireOp",EDGE,"E420"),sQuery(id+"F0.wireOp",EDGE,"E421"),sQuery(id+"F0.wireOp",EDGE,"E422"),sQuery(id+"F0.wireOp",EDGE,"E423"),sQuery(id+"F0.wireOp",EDGE,"E424"),sQuery(id+"F0.wireOp",EDGE,"E425"),sQuery(id+"F0.wireOp",EDGE,"E426"),sQuery(id+"F0.wireOp",EDGE,"E427"),sQuery(id+"F0.wireOp",EDGE,"E428"),sQuery(id+"F0.wireOp",EDGE,"E429"),sQuery(id+"F0.wireOp",EDGE,"E430"),sQuery(id+"F0.wireOp",EDGE,"E431"),sQuery(id+"F0.wireOp",EDGE,"E432"),sQuery(id+"F0.wireOp",EDGE,"E433"),sQuery(id+"F0.wireOp",EDGE,"E434"),sQuery(id+"F0.wireOp",EDGE,"E435"),sQuery(id+"F0.wireOp",EDGE,"E436"),sQuery(id+"F0.wireOp",EDGE,"E437"),sQuery(id+"F0.wireOp",EDGE,"E438"),sQuery(id+"F0.wireOp",EDGE,"E439"),sQuery(id+"F0.wireOp",EDGE,"E440"),sQuery(id+"F0.wireOp",EDGE,"E441"),sQuery(id+"F0.wireOp",EDGE,"E442"),sQuery(id+"F0.wireOp",EDGE,"E443"),sQuery(id+"F0.wireOp",EDGE,"E444"),sQuery(id+"F0.wireOp",EDGE,"E445"),sQuery(id+"F0.wireOp",EDGE,"E446"),sQuery(id+"F0.wireOp",EDGE,"E447"),sQuery(id+"F0.wireOp",EDGE,"E448"),sQuery(id+"F0.wireOp",EDGE,"E449"),sQuery(id+"F0.wireOp",EDGE,"E450"),sQuery(id+"F0.wireOp",EDGE,"E451"),sQuery(id+"F0.wireOp",EDGE,"E452"),sQuery(id+"F0.wireOp",EDGE,"E453"),sQuery(id+"F0.wireOp",EDGE,"E454"),sQuery(id+"F0.wireOp",EDGE,"E455"),sQuery(id+"F0.wireOp",EDGE,"E456"),sQuery(id+"F0.wireOp",EDGE,"E457"),sQuery(id+"F0.wireOp",EDGE,"E458"),sQuery(id+"F0.wireOp",EDGE,"E459"),sQuery(id+"F0.wireOp",EDGE,"E460"),sQuery(id+"F0.wireOp",EDGE,"E461"),sQuery(id+"F0.wireOp",EDGE,"E462"),sQuery(id+"F0.wireOp",EDGE,"E463"),sQuery(id+"F0.wireOp",EDGE,"E464"),sQuery(id+"F0.wireOp",EDGE,"E465"),sQuery(id+"F0.wireOp",EDGE,"E466"),sQuery(id+"F0.wireOp",EDGE,"E467"),sQuery(id+"F0.wireOp",EDGE,"E468"),sQuery(id+"F0.wireOp",EDGE,"E469"),sQuery(id+"F0.wireOp",EDGE,"E470"),sQuery(id+"F0.wireOp",EDGE,"E471"),sQuery(id+"F0.wireOp",EDGE,"E472"),sQuery(id+"F0.wireOp",EDGE,"E473"),sQuery(id+"F0.wireOp",EDGE,"E474"),sQuery(id+"F0.wireOp",EDGE,"E475"),sQuery(id+"F0.wireOp",EDGE,"E476"),sQuery(id+"F0.wireOp",EDGE,"E477"),sQuery(id+"F0.wireOp",EDGE,"E478"),sQuery(id+"F0.wireOp",EDGE,"E479"),sQuery(id+"F0.wireOp",EDGE,"E480"),sQuery(id+"F0.wireOp",EDGE,"E481"),sQuery(id+"F0.wireOp",EDGE,"E482"),sQuery(id+"F0.wireOp",EDGE,"E483"),sQuery(id+"F0.wireOp",EDGE,"E484"),sQuery(id+"F0.wireOp",EDGE,"E485"),sQuery(id+"F0.wireOp",EDGE,"E486"),sQuery(id+"F0.wireOp",EDGE,"E487"),sQuery(id+"F0.wireOp",EDGE,"E488"),sQuery(id+"F0.wireOp",EDGE,"E489"),sQuery(id+"F0.wireOp",EDGE,"E490"),sQuery(id+"F0.wireOp",EDGE,"E491"),sQuery(id+"F0.wireOp",EDGE,"E492"),sQuery(id+"F0.wireOp",EDGE,"E493"),sQuery(id+"F0.wireOp",EDGE,"E494"),sQuery(id+"F0.wireOp",EDGE,"E495"),sQuery(id+"F0.wireOp",EDGE,"E496"),sQuery(id+"F0.wireOp",EDGE,"E497"),sQuery(id+"F0.wireOp",EDGE,"E498"),sQuery(id+"F0.wireOp",EDGE,"E499"),sQuery(id+"F0.wireOp",EDGE,"E500"),sQuery(id+"F0.wireOp",EDGE,"E501"),sQuery(id+"F0.wireOp",EDGE,"E502"),sQuery(id+"F0.wireOp",EDGE,"E503")])]});
            var Q1;
            Q1=makeQuery(id+"F1.opExtrude","CAP_VERTEX",VERTEX,{"disambiguationData":[OSD([sQuery(id+"F0.wireOp",EDGE,"E47"),sQuery(id+"F0.wireOp",EDGE,"E48")])],"isStart":false});
            transform(context, id + "F2", {"entities" : qUnion([Q0]), "transformType" : TransformType.SCALE_UNIFORMLY, "scale" : 0.4, "scalePoint" : qUnion([Q1]), "makeCopy" : false});
        }
    });
